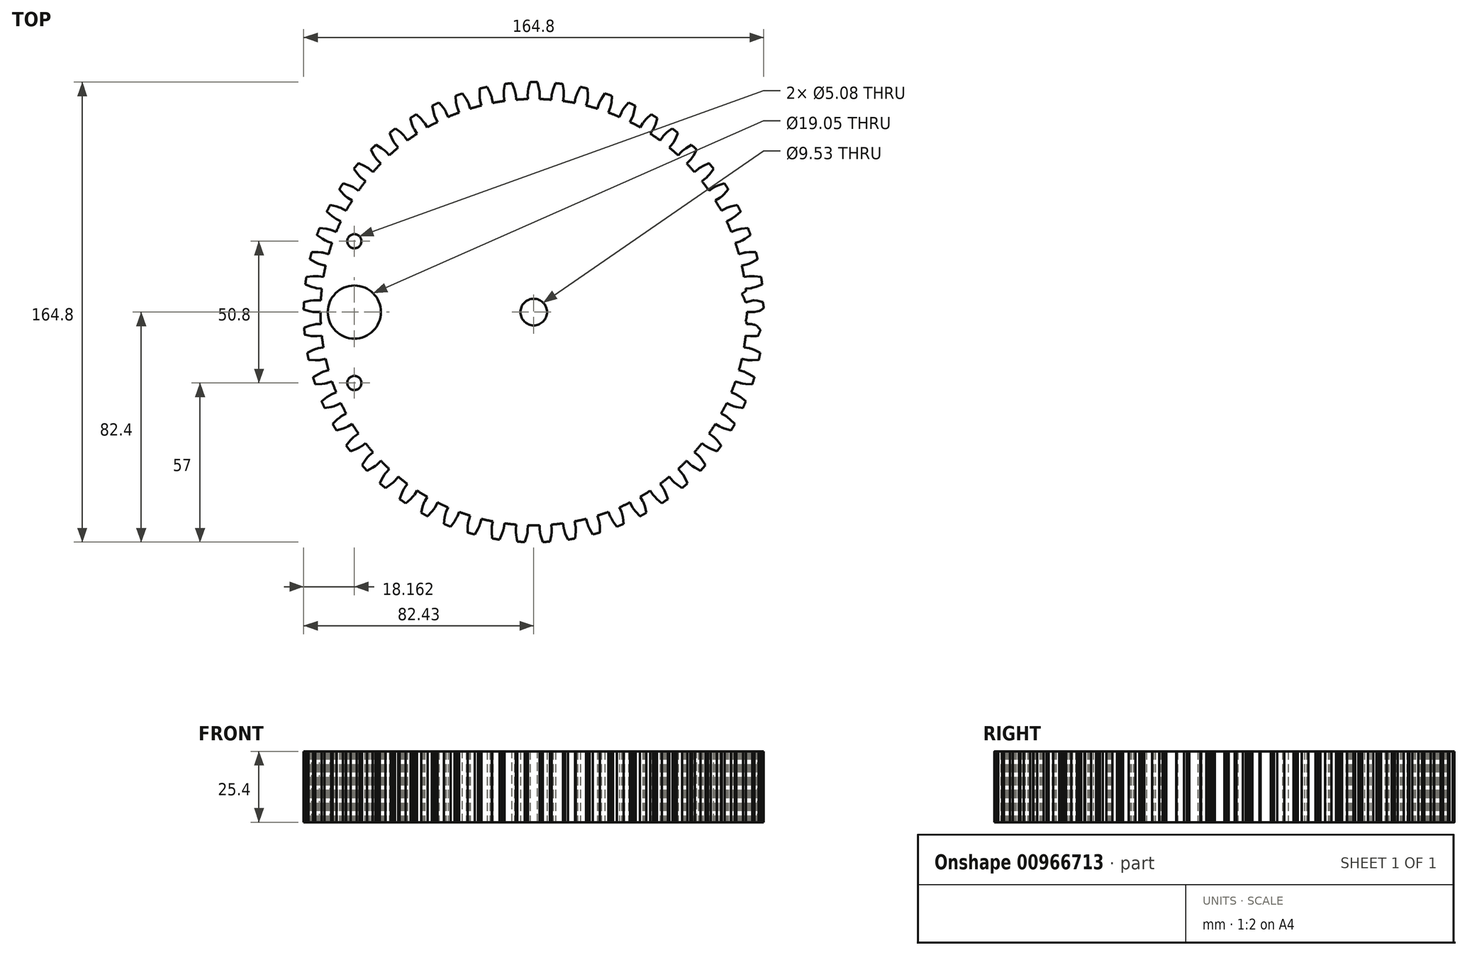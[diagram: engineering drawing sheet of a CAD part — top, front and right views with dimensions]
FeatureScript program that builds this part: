
annotation { "Feature Type Name" : "Feature", "Feature Type Description" : "" }
export const myFeature = defineFeature(function(context is Context, id is Id, definition is map)
    precondition{}
    {
        {
            var Q0;
            Q0=qCreatedBy(makeId("Top.planeOp"),FACE);
            var sketch = newSketch(context, id + "F0", { "sketchPlane" : qUnion([Q0])});
            skCircle(sketch, "E0", {"center": v(0, 0) * mm, "radius": 4.76 * mm});
            skArc(sketch, "E1", {"start": v(76.29, -4.24) * mm, "mid": v(76.37, -2.14) * mm, "end": v(76.4, -0.03) * mm});
            skLineSegment(sketch, "E2", {"start": v(76.4, -0.03) * mm, "end": v(78.17, -0.03) * mm});
            skLineSegment(sketch, "E3", {"start": v(78.17, -0.03) * mm, "end": v(78.19, -0.03) * mm});
            skLineSegment(sketch, "E4", {"start": v(78.19, -0.03) * mm, "end": v(78.2, -0.03) * mm});
            skLineSegment(sketch, "E5", {"start": v(78.2, -0.03) * mm, "end": v(78.26, -0.03) * mm});
            skLineSegment(sketch, "E6", {"start": v(78.26, -0.03) * mm, "end": v(78.37, -0.02) * mm});
            skLineSegment(sketch, "E7", {"start": v(78.37, -0.02) * mm, "end": v(78.6, 0) * mm});
            skLineSegment(sketch, "E8", {"start": v(78.6, 0) * mm, "end": v(79.09, 0.06) * mm});
            skLineSegment(sketch, "E9", {"start": v(79.09, 0.06) * mm, "end": v(80.16, 0.27) * mm});
            skLineSegment(sketch, "E10", {"start": v(80.16, 0.27) * mm, "end": v(82.43, 0.93) * mm});
            skArc(sketch, "E11", {"start": v(82.43, 0.93) * mm, "mid": v(82.4, 2.24) * mm, "end": v(82.35, 3.55) * mm});
            skLineSegment(sketch, "E12", {"start": v(78.06, 4.27) * mm, "end": v(78.07, 4.28) * mm});
            skLineSegment(sketch, "E13", {"start": v(78.07, 4.28) * mm, "end": v(78.09, 4.28) * mm});
            skLineSegment(sketch, "E14", {"start": v(78.09, 4.28) * mm, "end": v(78.14, 4.28) * mm});
            skLineSegment(sketch, "E15", {"start": v(78.14, 4.28) * mm, "end": v(78.25, 4.28) * mm});
            skLineSegment(sketch, "E16", {"start": v(78.25, 4.28) * mm, "end": v(78.47, 4.27) * mm});
            skLineSegment(sketch, "E17", {"start": v(78.47, 4.27) * mm, "end": v(78.97, 4.23) * mm});
            skLineSegment(sketch, "E18", {"start": v(78.97, 4.23) * mm, "end": v(80.05, 4.08) * mm});
            skLineSegment(sketch, "E19", {"start": v(80.05, 4.08) * mm, "end": v(82.35, 3.55) * mm});
            skLineSegment(sketch, "E20", {"start": v(76.29, 4.18) * mm, "end": v(78.06, 4.27) * mm});
            skArc(sketch, "E21", {"start": v(76.29, 4.18) * mm, "mid": v(76.14, 6.28) * mm, "end": v(75.94, 8.37) * mm});
            skLineSegment(sketch, "E22", {"start": v(75.94, 8.37) * mm, "end": v(77.7, 8.57) * mm});
            skLineSegment(sketch, "E23", {"start": v(77.7, 8.57) * mm, "end": v(77.71, 8.57) * mm});
            skLineSegment(sketch, "E24", {"start": v(77.71, 8.57) * mm, "end": v(77.73, 8.57) * mm});
            skLineSegment(sketch, "E25", {"start": v(77.73, 8.57) * mm, "end": v(77.78, 8.58) * mm});
            skLineSegment(sketch, "E26", {"start": v(77.78, 8.58) * mm, "end": v(77.89, 8.6) * mm});
            skLineSegment(sketch, "E27", {"start": v(77.89, 8.6) * mm, "end": v(78.11, 8.64) * mm});
            skLineSegment(sketch, "E28", {"start": v(78.11, 8.64) * mm, "end": v(78.6, 8.76) * mm});
            skLineSegment(sketch, "E29", {"start": v(78.6, 8.76) * mm, "end": v(79.64, 9.09) * mm});
            skLineSegment(sketch, "E30", {"start": v(79.64, 9.09) * mm, "end": v(81.82, 10) * mm});
            skArc(sketch, "E31", {"start": v(81.82, 10) * mm, "mid": v(81.65, 11.3) * mm, "end": v(81.46, 12.58) * mm});
            skLineSegment(sketch, "E32", {"start": v(77.1, 12.84) * mm, "end": v(77.12, 12.84) * mm});
            skLineSegment(sketch, "E33", {"start": v(77.12, 12.84) * mm, "end": v(77.14, 12.84) * mm});
            skLineSegment(sketch, "E34", {"start": v(77.14, 12.84) * mm, "end": v(77.2, 12.85) * mm});
            skLineSegment(sketch, "E35", {"start": v(77.2, 12.85) * mm, "end": v(77.3, 12.86) * mm});
            skLineSegment(sketch, "E36", {"start": v(77.3, 12.86) * mm, "end": v(77.52, 12.88) * mm});
            skLineSegment(sketch, "E37", {"start": v(77.52, 12.88) * mm, "end": v(78.03, 12.9) * mm});
            skLineSegment(sketch, "E38", {"start": v(78.03, 12.9) * mm, "end": v(79.11, 12.86) * mm});
            skLineSegment(sketch, "E39", {"start": v(79.11, 12.86) * mm, "end": v(81.46, 12.58) * mm});
            skLineSegment(sketch, "E40", {"start": v(75.36, 12.54) * mm, "end": v(77.1, 12.84) * mm});
            skArc(sketch, "E41", {"start": v(75.36, 12.54) * mm, "mid": v(74.99, 14.62) * mm, "end": v(74.55, 16.68) * mm});
            skLineSegment(sketch, "E42", {"start": v(74.55, 16.68) * mm, "end": v(76.28, 17.06) * mm});
            skLineSegment(sketch, "E43", {"start": v(76.28, 17.06) * mm, "end": v(76.3, 17.07) * mm});
            skLineSegment(sketch, "E44", {"start": v(76.3, 17.07) * mm, "end": v(76.31, 17.07) * mm});
            skLineSegment(sketch, "E45", {"start": v(76.31, 17.07) * mm, "end": v(76.36, 17.08) * mm});
            skLineSegment(sketch, "E46", {"start": v(76.36, 17.08) * mm, "end": v(76.47, 17.11) * mm});
            skLineSegment(sketch, "E47", {"start": v(76.47, 17.11) * mm, "end": v(76.68, 17.18) * mm});
            skLineSegment(sketch, "E48", {"start": v(76.68, 17.18) * mm, "end": v(77.15, 17.36) * mm});
            skLineSegment(sketch, "E49", {"start": v(77.15, 17.36) * mm, "end": v(78.15, 17.8) * mm});
            skLineSegment(sketch, "E50", {"start": v(78.15, 17.8) * mm, "end": v(80.22, 18.93) * mm});
            skArc(sketch, "E51", {"start": v(80.22, 18.93) * mm, "mid": v(79.9, 20.2) * mm, "end": v(79.58, 21.47) * mm});
            skLineSegment(sketch, "E52", {"start": v(75.22, 21.24) * mm, "end": v(75.24, 21.24) * mm});
            skLineSegment(sketch, "E53", {"start": v(75.24, 21.24) * mm, "end": v(75.26, 21.25) * mm});
            skLineSegment(sketch, "E54", {"start": v(75.26, 21.25) * mm, "end": v(75.3, 21.26) * mm});
            skLineSegment(sketch, "E55", {"start": v(75.3, 21.26) * mm, "end": v(75.41, 21.28) * mm});
            skLineSegment(sketch, "E56", {"start": v(75.41, 21.28) * mm, "end": v(75.63, 21.33) * mm});
            skLineSegment(sketch, "E57", {"start": v(75.63, 21.33) * mm, "end": v(76.13, 21.4) * mm});
            skLineSegment(sketch, "E58", {"start": v(76.13, 21.4) * mm, "end": v(77.22, 21.49) * mm});
            skLineSegment(sketch, "E59", {"start": v(77.22, 21.49) * mm, "end": v(79.58, 21.47) * mm});
            skLineSegment(sketch, "E60", {"start": v(73.52, 20.76) * mm, "end": v(75.22, 21.24) * mm});
            skArc(sketch, "E61", {"start": v(73.52, 20.76) * mm, "mid": v(72.92, 22.78) * mm, "end": v(72.26, 24.78) * mm});
            skLineSegment(sketch, "E62", {"start": v(72.26, 24.78) * mm, "end": v(73.94, 25.35) * mm});
            skLineSegment(sketch, "E63", {"start": v(73.94, 25.35) * mm, "end": v(73.95, 25.36) * mm});
            skLineSegment(sketch, "E64", {"start": v(73.95, 25.36) * mm, "end": v(73.97, 25.36) * mm});
            skLineSegment(sketch, "E65", {"start": v(73.97, 25.36) * mm, "end": v(74.02, 25.38) * mm});
            skLineSegment(sketch, "E66", {"start": v(74.02, 25.38) * mm, "end": v(74.12, 25.42) * mm});
            skLineSegment(sketch, "E67", {"start": v(74.12, 25.42) * mm, "end": v(74.32, 25.51) * mm});
            skLineSegment(sketch, "E68", {"start": v(74.32, 25.51) * mm, "end": v(74.77, 25.74) * mm});
            skLineSegment(sketch, "E69", {"start": v(74.77, 25.74) * mm, "end": v(75.72, 26.28) * mm});
            skLineSegment(sketch, "E70", {"start": v(75.72, 26.28) * mm, "end": v(77.65, 27.64) * mm});
            skArc(sketch, "E71", {"start": v(77.65, 27.64) * mm, "mid": v(77.2, 28.87) * mm, "end": v(76.73, 30.1) * mm});
            skLineSegment(sketch, "E72", {"start": v(72.43, 29.39) * mm, "end": v(72.44, 29.39) * mm});
            skLineSegment(sketch, "E73", {"start": v(72.44, 29.39) * mm, "end": v(72.46, 29.4) * mm});
            skLineSegment(sketch, "E74", {"start": v(72.46, 29.4) * mm, "end": v(72.5, 29.41) * mm});
            skLineSegment(sketch, "E75", {"start": v(72.5, 29.41) * mm, "end": v(72.6, 29.45) * mm});
            skLineSegment(sketch, "E76", {"start": v(72.6, 29.45) * mm, "end": v(72.83, 29.52) * mm});
            skLineSegment(sketch, "E77", {"start": v(72.83, 29.52) * mm, "end": v(73.31, 29.64) * mm});
            skLineSegment(sketch, "E78", {"start": v(73.31, 29.64) * mm, "end": v(74.38, 29.85) * mm});
            skLineSegment(sketch, "E79", {"start": v(74.38, 29.85) * mm, "end": v(76.73, 30.1) * mm});
            skLineSegment(sketch, "E80", {"start": v(70.79, 28.72) * mm, "end": v(72.43, 29.39) * mm});
            skArc(sketch, "E81", {"start": v(70.79, 28.72) * mm, "mid": v(69.97, 30.66) * mm, "end": v(69.1, 32.58) * mm});
            skLineSegment(sketch, "E82", {"start": v(69.1, 32.58) * mm, "end": v(70.7, 33.33) * mm});
            skLineSegment(sketch, "E83", {"start": v(70.7, 33.33) * mm, "end": v(70.7, 33.34) * mm});
            skLineSegment(sketch, "E84", {"start": v(70.7, 33.34) * mm, "end": v(70.73, 33.35) * mm});
            skLineSegment(sketch, "E85", {"start": v(70.73, 33.35) * mm, "end": v(70.77, 33.37) * mm});
            skLineSegment(sketch, "E86", {"start": v(70.77, 33.37) * mm, "end": v(70.87, 33.42) * mm});
            skLineSegment(sketch, "E87", {"start": v(70.87, 33.42) * mm, "end": v(71.06, 33.54) * mm});
            skLineSegment(sketch, "E88", {"start": v(71.06, 33.54) * mm, "end": v(71.48, 33.8) * mm});
            skLineSegment(sketch, "E89", {"start": v(71.48, 33.8) * mm, "end": v(72.36, 34.45) * mm});
            skLineSegment(sketch, "E90", {"start": v(72.36, 34.45) * mm, "end": v(74.13, 36.02) * mm});
            skArc(sketch, "E91", {"start": v(74.13, 36.02) * mm, "mid": v(73.55, 37.19) * mm, "end": v(72.95, 38.35) * mm});
            skLineSegment(sketch, "E92", {"start": v(68.75, 37.17) * mm, "end": v(68.76, 37.18) * mm});
            skLineSegment(sketch, "E93", {"start": v(68.76, 37.18) * mm, "end": v(68.78, 37.19) * mm});
            skLineSegment(sketch, "E94", {"start": v(68.78, 37.19) * mm, "end": v(68.83, 37.21) * mm});
            skLineSegment(sketch, "E95", {"start": v(68.83, 37.21) * mm, "end": v(68.93, 37.26) * mm});
            skLineSegment(sketch, "E96", {"start": v(68.93, 37.26) * mm, "end": v(69.13, 37.35) * mm});
            skLineSegment(sketch, "E97", {"start": v(69.13, 37.35) * mm, "end": v(69.6, 37.53) * mm});
            skLineSegment(sketch, "E98", {"start": v(69.6, 37.53) * mm, "end": v(70.64, 37.85) * mm});
            skLineSegment(sketch, "E99", {"start": v(70.64, 37.85) * mm, "end": v(72.95, 38.35) * mm});
            skLineSegment(sketch, "E100", {"start": v(67.2, 36.33) * mm, "end": v(68.75, 37.17) * mm});
            skArc(sketch, "E101", {"start": v(67.2, 36.33) * mm, "mid": v(66.17, 38.17) * mm, "end": v(65.1, 39.98) * mm});
            skLineSegment(sketch, "E102", {"start": v(65.1, 39.98) * mm, "end": v(66.6, 40.9) * mm});
            skLineSegment(sketch, "E103", {"start": v(66.6, 40.9) * mm, "end": v(66.6, 40.91) * mm});
            skLineSegment(sketch, "E104", {"start": v(66.6, 40.91) * mm, "end": v(66.62, 40.92) * mm});
            skLineSegment(sketch, "E105", {"start": v(66.62, 40.92) * mm, "end": v(66.67, 40.95) * mm});
            skLineSegment(sketch, "E106", {"start": v(66.67, 40.95) * mm, "end": v(66.76, 41.01) * mm});
            skLineSegment(sketch, "E107", {"start": v(66.76, 41.01) * mm, "end": v(66.94, 41.15) * mm});
            skLineSegment(sketch, "E108", {"start": v(66.94, 41.15) * mm, "end": v(67.33, 41.47) * mm});
            skLineSegment(sketch, "E109", {"start": v(67.33, 41.47) * mm, "end": v(68.13, 42.2) * mm});
            skLineSegment(sketch, "E110", {"start": v(68.13, 42.2) * mm, "end": v(69.71, 43.95) * mm});
            skArc(sketch, "E111", {"start": v(69.71, 43.95) * mm, "mid": v(69, 45.05) * mm, "end": v(68.29, 46.14) * mm});
            skLineSegment(sketch, "E112", {"start": v(64.24, 44.51) * mm, "end": v(64.25, 44.52) * mm});
            skLineSegment(sketch, "E113", {"start": v(64.25, 44.52) * mm, "end": v(64.27, 44.53) * mm});
            skLineSegment(sketch, "E114", {"start": v(64.27, 44.53) * mm, "end": v(64.31, 44.56) * mm});
            skLineSegment(sketch, "E115", {"start": v(64.31, 44.56) * mm, "end": v(64.4, 44.61) * mm});
            skLineSegment(sketch, "E116", {"start": v(64.4, 44.61) * mm, "end": v(64.6, 44.73) * mm});
            skLineSegment(sketch, "E117", {"start": v(64.6, 44.73) * mm, "end": v(65.05, 44.96) * mm});
            skLineSegment(sketch, "E118", {"start": v(65.05, 44.96) * mm, "end": v(66.04, 45.4) * mm});
            skLineSegment(sketch, "E119", {"start": v(66.04, 45.4) * mm, "end": v(68.29, 46.14) * mm});
            skLineSegment(sketch, "E120", {"start": v(62.79, 43.5) * mm, "end": v(64.24, 44.51) * mm});
            skArc(sketch, "E121", {"start": v(62.79, 43.5) * mm, "mid": v(61.56, 45.22) * mm, "end": v(60.3, 46.9) * mm});
            skLineSegment(sketch, "E122", {"start": v(60.3, 46.9) * mm, "end": v(61.7, 47.98) * mm});
            skLineSegment(sketch, "E123", {"start": v(61.7, 47.98) * mm, "end": v(61.7, 48) * mm});
            skLineSegment(sketch, "E124", {"start": v(61.7, 48) * mm, "end": v(61.71, 48) * mm});
            skLineSegment(sketch, "E125", {"start": v(61.71, 48) * mm, "end": v(61.75, 48.04) * mm});
            skLineSegment(sketch, "E126", {"start": v(61.75, 48.04) * mm, "end": v(61.84, 48.1) * mm});
            skLineSegment(sketch, "E127", {"start": v(61.84, 48.1) * mm, "end": v(62, 48.26) * mm});
            skLineSegment(sketch, "E128", {"start": v(62, 48.26) * mm, "end": v(62.35, 48.62) * mm});
            skLineSegment(sketch, "E129", {"start": v(62.35, 48.62) * mm, "end": v(63.07, 49.44) * mm});
            skLineSegment(sketch, "E130", {"start": v(63.07, 49.44) * mm, "end": v(64.45, 51.36) * mm});
            skArc(sketch, "E131", {"start": v(64.45, 51.36) * mm, "mid": v(63.63, 52.37) * mm, "end": v(62.8, 53.37) * mm});
            skLineSegment(sketch, "E132", {"start": v(58.95, 51.3) * mm, "end": v(58.96, 51.32) * mm});
            skLineSegment(sketch, "E133", {"start": v(58.96, 51.32) * mm, "end": v(58.98, 51.33) * mm});
            skLineSegment(sketch, "E134", {"start": v(58.98, 51.33) * mm, "end": v(59.02, 51.36) * mm});
            skLineSegment(sketch, "E135", {"start": v(59.02, 51.36) * mm, "end": v(59.1, 51.43) * mm});
            skLineSegment(sketch, "E136", {"start": v(59.1, 51.43) * mm, "end": v(59.29, 51.56) * mm});
            skLineSegment(sketch, "E137", {"start": v(59.29, 51.56) * mm, "end": v(59.7, 51.84) * mm});
            skLineSegment(sketch, "E138", {"start": v(59.7, 51.84) * mm, "end": v(60.65, 52.38) * mm});
            skLineSegment(sketch, "E139", {"start": v(60.65, 52.38) * mm, "end": v(62.8, 53.37) * mm});
            skLineSegment(sketch, "E140", {"start": v(57.62, 50.15) * mm, "end": v(58.95, 51.3) * mm});
            skArc(sketch, "E141", {"start": v(57.62, 50.15) * mm, "mid": v(56.21, 51.72) * mm, "end": v(54.77, 53.24) * mm});
            skLineSegment(sketch, "E142", {"start": v(54.77, 53.24) * mm, "end": v(56.03, 54.48) * mm});
            skLineSegment(sketch, "E143", {"start": v(56.03, 54.48) * mm, "end": v(56.04, 54.49) * mm});
            skLineSegment(sketch, "E144", {"start": v(56.04, 54.49) * mm, "end": v(56.06, 54.5) * mm});
            skLineSegment(sketch, "E145", {"start": v(56.06, 54.5) * mm, "end": v(56.1, 54.54) * mm});
            skLineSegment(sketch, "E146", {"start": v(56.1, 54.54) * mm, "end": v(56.17, 54.62) * mm});
            skLineSegment(sketch, "E147", {"start": v(56.17, 54.62) * mm, "end": v(56.31, 54.8) * mm});
            skLineSegment(sketch, "E148", {"start": v(56.31, 54.8) * mm, "end": v(56.62, 55.18) * mm});
            skLineSegment(sketch, "E149", {"start": v(56.62, 55.18) * mm, "end": v(57.24, 56.08) * mm});
            skLineSegment(sketch, "E150", {"start": v(57.24, 56.08) * mm, "end": v(58.4, 58.13) * mm});
            skArc(sketch, "E151", {"start": v(58.4, 58.13) * mm, "mid": v(57.48, 59.05) * mm, "end": v(56.53, 59.96) * mm});
            skLineSegment(sketch, "E152", {"start": v(52.95, 57.48) * mm, "end": v(52.95, 57.5) * mm});
            skLineSegment(sketch, "E153", {"start": v(52.95, 57.5) * mm, "end": v(52.97, 57.5) * mm});
            skLineSegment(sketch, "E154", {"start": v(52.97, 57.5) * mm, "end": v(53, 57.54) * mm});
            skLineSegment(sketch, "E155", {"start": v(53, 57.54) * mm, "end": v(53.08, 57.62) * mm});
            skLineSegment(sketch, "E156", {"start": v(53.08, 57.62) * mm, "end": v(53.25, 57.77) * mm});
            skLineSegment(sketch, "E157", {"start": v(53.25, 57.77) * mm, "end": v(53.63, 58.1) * mm});
            skLineSegment(sketch, "E158", {"start": v(53.63, 58.1) * mm, "end": v(54.51, 58.74) * mm});
            skLineSegment(sketch, "E159", {"start": v(54.51, 58.74) * mm, "end": v(56.53, 59.96) * mm});
            skLineSegment(sketch, "E160", {"start": v(51.75, 56.18) * mm, "end": v(52.95, 57.48) * mm});
            skArc(sketch, "E161", {"start": v(51.75, 56.18) * mm, "mid": v(50.18, 57.58) * mm, "end": v(48.57, 58.95) * mm});
            skLineSegment(sketch, "E162", {"start": v(48.57, 58.95) * mm, "end": v(49.7, 60.31) * mm});
            skLineSegment(sketch, "E163", {"start": v(49.7, 60.31) * mm, "end": v(49.7, 60.32) * mm});
            skLineSegment(sketch, "E164", {"start": v(49.7, 60.32) * mm, "end": v(49.72, 60.34) * mm});
            skLineSegment(sketch, "E165", {"start": v(49.72, 60.34) * mm, "end": v(49.75, 60.38) * mm});
            skLineSegment(sketch, "E166", {"start": v(49.75, 60.38) * mm, "end": v(49.81, 60.47) * mm});
            skLineSegment(sketch, "E167", {"start": v(49.81, 60.47) * mm, "end": v(49.94, 60.65) * mm});
            skLineSegment(sketch, "E168", {"start": v(49.94, 60.65) * mm, "end": v(50.2, 61.08) * mm});
            skLineSegment(sketch, "E169", {"start": v(50.2, 61.08) * mm, "end": v(50.72, 62.04) * mm});
            skLineSegment(sketch, "E170", {"start": v(50.72, 62.04) * mm, "end": v(51.66, 64.2) * mm});
            skArc(sketch, "E171", {"start": v(51.66, 64.2) * mm, "mid": v(50.63, 65.02) * mm, "end": v(49.6, 65.81) * mm});
            skLineSegment(sketch, "E172", {"start": v(46.3, 62.96) * mm, "end": v(46.3, 62.97) * mm});
            skLineSegment(sketch, "E173", {"start": v(46.3, 62.97) * mm, "end": v(46.32, 62.98) * mm});
            skLineSegment(sketch, "E174", {"start": v(46.32, 62.98) * mm, "end": v(46.35, 63.02) * mm});
            skLineSegment(sketch, "E175", {"start": v(46.35, 63.02) * mm, "end": v(46.42, 63.1) * mm});
            skLineSegment(sketch, "E176", {"start": v(46.42, 63.1) * mm, "end": v(46.57, 63.28) * mm});
            skLineSegment(sketch, "E177", {"start": v(46.57, 63.28) * mm, "end": v(46.92, 63.64) * mm});
            skLineSegment(sketch, "E178", {"start": v(46.92, 63.64) * mm, "end": v(47.72, 64.38) * mm});
            skLineSegment(sketch, "E179", {"start": v(47.72, 64.38) * mm, "end": v(49.6, 65.81) * mm});
            skLineSegment(sketch, "E180", {"start": v(45.25, 61.53) * mm, "end": v(46.3, 62.96) * mm});
            skArc(sketch, "E181", {"start": v(45.25, 61.53) * mm, "mid": v(43.54, 62.76) * mm, "end": v(41.79, 63.93) * mm});
            skLineSegment(sketch, "E182", {"start": v(41.79, 63.93) * mm, "end": v(42.76, 65.41) * mm});
            skLineSegment(sketch, "E183", {"start": v(42.76, 65.41) * mm, "end": v(42.76, 65.42) * mm});
            skLineSegment(sketch, "E184", {"start": v(42.76, 65.42) * mm, "end": v(42.77, 65.44) * mm});
            skLineSegment(sketch, "E185", {"start": v(42.77, 65.44) * mm, "end": v(42.8, 65.48) * mm});
            skLineSegment(sketch, "E186", {"start": v(42.8, 65.48) * mm, "end": v(42.85, 65.58) * mm});
            skLineSegment(sketch, "E187", {"start": v(42.85, 65.58) * mm, "end": v(42.96, 65.78) * mm});
            skLineSegment(sketch, "E188", {"start": v(42.96, 65.78) * mm, "end": v(43.18, 66.23) * mm});
            skLineSegment(sketch, "E189", {"start": v(43.18, 66.23) * mm, "end": v(43.59, 67.24) * mm});
            skLineSegment(sketch, "E190", {"start": v(43.59, 67.24) * mm, "end": v(44.28, 69.5) * mm});
            skArc(sketch, "E191", {"start": v(44.28, 69.5) * mm, "mid": v(43.17, 70.2) * mm, "end": v(42.05, 70.87) * mm});
            skLineSegment(sketch, "E192", {"start": v(39.09, 67.67) * mm, "end": v(39.1, 67.68) * mm});
            skLineSegment(sketch, "E193", {"start": v(39.1, 67.68) * mm, "end": v(39.1, 67.7) * mm});
            skLineSegment(sketch, "E194", {"start": v(39.1, 67.7) * mm, "end": v(39.13, 67.74) * mm});
            skLineSegment(sketch, "E195", {"start": v(39.13, 67.74) * mm, "end": v(39.2, 67.83) * mm});
            skLineSegment(sketch, "E196", {"start": v(39.2, 67.83) * mm, "end": v(39.32, 68.02) * mm});
            skLineSegment(sketch, "E197", {"start": v(39.32, 68.02) * mm, "end": v(39.63, 68.41) * mm});
            skLineSegment(sketch, "E198", {"start": v(39.63, 68.41) * mm, "end": v(40.34, 69.24) * mm});
            skLineSegment(sketch, "E199", {"start": v(40.34, 69.24) * mm, "end": v(42.05, 70.87) * mm});
            skLineSegment(sketch, "E200", {"start": v(38.2, 66.14) * mm, "end": v(39.09, 67.67) * mm});
            skArc(sketch, "E201", {"start": v(38.2, 66.14) * mm, "mid": v(36.36, 67.16) * mm, "end": v(34.5, 68.14) * mm});
            skLineSegment(sketch, "E202", {"start": v(34.5, 68.14) * mm, "end": v(35.3, 69.72) * mm});
            skLineSegment(sketch, "E203", {"start": v(35.3, 69.72) * mm, "end": v(35.3, 69.73) * mm});
            skLineSegment(sketch, "E204", {"start": v(35.3, 69.73) * mm, "end": v(35.31, 69.75) * mm});
            skLineSegment(sketch, "E205", {"start": v(35.31, 69.75) * mm, "end": v(35.33, 69.8) * mm});
            skLineSegment(sketch, "E206", {"start": v(35.33, 69.8) * mm, "end": v(35.38, 69.9) * mm});
            skLineSegment(sketch, "E207", {"start": v(35.38, 69.9) * mm, "end": v(35.46, 70.1) * mm});
            skLineSegment(sketch, "E208", {"start": v(35.46, 70.1) * mm, "end": v(35.63, 70.58) * mm});
            skLineSegment(sketch, "E209", {"start": v(35.63, 70.58) * mm, "end": v(35.92, 71.63) * mm});
            skLineSegment(sketch, "E210", {"start": v(35.92, 71.63) * mm, "end": v(36.36, 73.95) * mm});
            skArc(sketch, "E211", {"start": v(36.36, 73.95) * mm, "mid": v(35.18, 74.52) * mm, "end": v(34, 75.06) * mm});
            skLineSegment(sketch, "E212", {"start": v(31.4, 71.56) * mm, "end": v(31.4, 71.57) * mm});
            skLineSegment(sketch, "E213", {"start": v(31.4, 71.57) * mm, "end": v(31.42, 71.59) * mm});
            skLineSegment(sketch, "E214", {"start": v(31.42, 71.59) * mm, "end": v(31.44, 71.63) * mm});
            skLineSegment(sketch, "E215", {"start": v(31.44, 71.63) * mm, "end": v(31.49, 71.73) * mm});
            skLineSegment(sketch, "E216", {"start": v(31.49, 71.73) * mm, "end": v(31.6, 71.93) * mm});
            skLineSegment(sketch, "E217", {"start": v(31.6, 71.93) * mm, "end": v(31.86, 72.36) * mm});
            skLineSegment(sketch, "E218", {"start": v(31.86, 72.36) * mm, "end": v(32.48, 73.25) * mm});
            skLineSegment(sketch, "E219", {"start": v(32.48, 73.25) * mm, "end": v(34, 75.06) * mm});
            skLineSegment(sketch, "E220", {"start": v(30.7, 69.94) * mm, "end": v(31.4, 71.56) * mm});
            skArc(sketch, "E221", {"start": v(30.7, 69.94) * mm, "mid": v(28.75, 70.76) * mm, "end": v(26.8, 71.52) * mm});
            skLineSegment(sketch, "E222", {"start": v(26.8, 71.52) * mm, "end": v(27.41, 73.18) * mm});
            skLineSegment(sketch, "E223", {"start": v(27.41, 73.18) * mm, "end": v(27.41, 73.19) * mm});
            skLineSegment(sketch, "E224", {"start": v(27.41, 73.19) * mm, "end": v(27.42, 73.2) * mm});
            skLineSegment(sketch, "E225", {"start": v(27.42, 73.2) * mm, "end": v(27.44, 73.26) * mm});
            skLineSegment(sketch, "E226", {"start": v(27.44, 73.26) * mm, "end": v(27.47, 73.36) * mm});
            skLineSegment(sketch, "E227", {"start": v(27.47, 73.36) * mm, "end": v(27.53, 73.58) * mm});
            skLineSegment(sketch, "E228", {"start": v(27.53, 73.58) * mm, "end": v(27.64, 74.07) * mm});
            skLineSegment(sketch, "E229", {"start": v(27.64, 74.07) * mm, "end": v(27.82, 75.14) * mm});
            skLineSegment(sketch, "E230", {"start": v(27.82, 75.14) * mm, "end": v(28, 77.5) * mm});
            skArc(sketch, "E231", {"start": v(28, 77.5) * mm, "mid": v(26.77, 77.93) * mm, "end": v(25.53, 78.35) * mm});
            skLineSegment(sketch, "E232", {"start": v(23.34, 74.58) * mm, "end": v(23.34, 74.59) * mm});
            skLineSegment(sketch, "E233", {"start": v(23.34, 74.59) * mm, "end": v(23.35, 74.6) * mm});
            skLineSegment(sketch, "E234", {"start": v(23.35, 74.6) * mm, "end": v(23.36, 74.66) * mm});
            skLineSegment(sketch, "E235", {"start": v(23.36, 74.66) * mm, "end": v(23.4, 74.76) * mm});
            skLineSegment(sketch, "E236", {"start": v(23.4, 74.76) * mm, "end": v(23.49, 74.97) * mm});
            skLineSegment(sketch, "E237", {"start": v(23.49, 74.97) * mm, "end": v(23.7, 75.42) * mm});
            skLineSegment(sketch, "E238", {"start": v(23.7, 75.42) * mm, "end": v(24.22, 76.38) * mm});
            skLineSegment(sketch, "E239", {"start": v(24.22, 76.38) * mm, "end": v(25.53, 78.35) * mm});
            skLineSegment(sketch, "E240", {"start": v(22.8, 72.89) * mm, "end": v(23.34, 74.58) * mm});
            skArc(sketch, "E241", {"start": v(22.8, 72.89) * mm, "mid": v(20.79, 73.49) * mm, "end": v(18.76, 74.03) * mm});
            skLineSegment(sketch, "E242", {"start": v(18.76, 74.03) * mm, "end": v(19.2, 75.75) * mm});
            skLineSegment(sketch, "E243", {"start": v(19.2, 75.75) * mm, "end": v(19.2, 75.76) * mm});
            skLineSegment(sketch, "E244", {"start": v(19.2, 75.76) * mm, "end": v(19.2, 75.78) * mm});
            skLineSegment(sketch, "E245", {"start": v(19.2, 75.78) * mm, "end": v(19.2, 75.83) * mm});
            skLineSegment(sketch, "E246", {"start": v(19.2, 75.83) * mm, "end": v(19.23, 75.94) * mm});
            skLineSegment(sketch, "E247", {"start": v(19.23, 75.94) * mm, "end": v(19.27, 76.16) * mm});
            skLineSegment(sketch, "E248", {"start": v(19.27, 76.16) * mm, "end": v(19.32, 76.66) * mm});
            skLineSegment(sketch, "E249", {"start": v(19.32, 76.66) * mm, "end": v(19.38, 77.75) * mm});
            skLineSegment(sketch, "E250", {"start": v(19.38, 77.75) * mm, "end": v(19.3, 80.1) * mm});
            skArc(sketch, "E251", {"start": v(19.3, 80.1) * mm, "mid": v(18.03, 80.4) * mm, "end": v(16.75, 80.68) * mm});
            skLineSegment(sketch, "E252", {"start": v(14.99, 76.7) * mm, "end": v(14.99, 76.7) * mm});
            skLineSegment(sketch, "E253", {"start": v(14.99, 76.7) * mm, "end": v(15, 76.72) * mm});
            skLineSegment(sketch, "E254", {"start": v(15, 76.72) * mm, "end": v(15, 76.77) * mm});
            skLineSegment(sketch, "E255", {"start": v(15, 76.77) * mm, "end": v(15.03, 76.88) * mm});
            skLineSegment(sketch, "E256", {"start": v(15.03, 76.88) * mm, "end": v(15.1, 77.1) * mm});
            skLineSegment(sketch, "E257", {"start": v(15.1, 77.1) * mm, "end": v(15.25, 77.57) * mm});
            skLineSegment(sketch, "E258", {"start": v(15.25, 77.57) * mm, "end": v(15.66, 78.58) * mm});
            skLineSegment(sketch, "E259", {"start": v(15.66, 78.58) * mm, "end": v(16.75, 80.68) * mm});
            skLineSegment(sketch, "E260", {"start": v(14.65, 74.96) * mm, "end": v(14.99, 76.7) * mm});
            skArc(sketch, "E261", {"start": v(14.65, 74.96) * mm, "mid": v(12.58, 75.33) * mm, "end": v(10.5, 75.65) * mm});
            skLineSegment(sketch, "E262", {"start": v(10.5, 75.65) * mm, "end": v(10.74, 77.4) * mm});
            skLineSegment(sketch, "E263", {"start": v(10.74, 77.4) * mm, "end": v(10.74, 77.41) * mm});
            skLineSegment(sketch, "E264", {"start": v(10.74, 77.41) * mm, "end": v(10.74, 77.43) * mm});
            skLineSegment(sketch, "E265", {"start": v(10.74, 77.43) * mm, "end": v(10.75, 77.48) * mm});
            skLineSegment(sketch, "E266", {"start": v(10.75, 77.48) * mm, "end": v(10.76, 77.6) * mm});
            skLineSegment(sketch, "E267", {"start": v(10.76, 77.6) * mm, "end": v(10.77, 77.82) * mm});
            skLineSegment(sketch, "E268", {"start": v(10.77, 77.82) * mm, "end": v(10.77, 78.32) * mm});
            skLineSegment(sketch, "E269", {"start": v(10.77, 78.32) * mm, "end": v(10.71, 79.4) * mm});
            skLineSegment(sketch, "E270", {"start": v(10.71, 79.4) * mm, "end": v(10.37, 81.75) * mm});
            skArc(sketch, "E271", {"start": v(10.37, 81.75) * mm, "mid": v(9.07, 81.9) * mm, "end": v(7.77, 82.03) * mm});
            skLineSegment(sketch, "E272", {"start": v(6.46, 77.88) * mm, "end": v(6.46, 77.89) * mm});
            skLineSegment(sketch, "E273", {"start": v(6.46, 77.89) * mm, "end": v(6.46, 77.9) * mm});
            skLineSegment(sketch, "E274", {"start": v(6.46, 77.9) * mm, "end": v(6.47, 77.96) * mm});
            skLineSegment(sketch, "E275", {"start": v(6.47, 77.96) * mm, "end": v(6.48, 78.07) * mm});
            skLineSegment(sketch, "E276", {"start": v(6.48, 78.07) * mm, "end": v(6.52, 78.29) * mm});
            skLineSegment(sketch, "E277", {"start": v(6.52, 78.29) * mm, "end": v(6.62, 78.78) * mm});
            skLineSegment(sketch, "E278", {"start": v(6.62, 78.78) * mm, "end": v(6.92, 79.83) * mm});
            skLineSegment(sketch, "E279", {"start": v(6.92, 79.83) * mm, "end": v(7.77, 82.03) * mm});
            skLineSegment(sketch, "E280", {"start": v(6.3, 76.11) * mm, "end": v(6.46, 77.88) * mm});
            skArc(sketch, "E281", {"start": v(6.3, 76.11) * mm, "mid": v(4.2, 76.26) * mm, "end": v(2.1, 76.34) * mm});
            skLineSegment(sketch, "E282", {"start": v(2.1, 76.34) * mm, "end": v(2.15, 78.11) * mm});
            skLineSegment(sketch, "E283", {"start": v(2.15, 78.11) * mm, "end": v(2.15, 78.12) * mm});
            skLineSegment(sketch, "E284", {"start": v(2.15, 78.12) * mm, "end": v(2.15, 78.14) * mm});
            skLineSegment(sketch, "E285", {"start": v(2.15, 78.14) * mm, "end": v(2.15, 78.2) * mm});
            skLineSegment(sketch, "E286", {"start": v(2.15, 78.2) * mm, "end": v(2.15, 78.3) * mm});
            skLineSegment(sketch, "E287", {"start": v(2.15, 78.3) * mm, "end": v(2.14, 78.53) * mm});
            skLineSegment(sketch, "E288", {"start": v(2.14, 78.53) * mm, "end": v(2.09, 79.03) * mm});
            skLineSegment(sketch, "E289", {"start": v(2.09, 79.03) * mm, "end": v(1.9, 80.1) * mm});
            skLineSegment(sketch, "E290", {"start": v(1.9, 80.1) * mm, "end": v(1.3, 82.39) * mm});
            skArc(sketch, "E291", {"start": v(1.3, 82.39) * mm, "mid": v(0, 82.4) * mm, "end": v(-1.3, 82.39) * mm});
            skLineSegment(sketch, "E292", {"start": v(-2.15, 78.11) * mm, "end": v(-2.15, 78.12) * mm});
            skLineSegment(sketch, "E293", {"start": v(-2.15, 78.12) * mm, "end": v(-2.15, 78.14) * mm});
            skLineSegment(sketch, "E294", {"start": v(-2.15, 78.14) * mm, "end": v(-2.15, 78.2) * mm});
            skLineSegment(sketch, "E295", {"start": v(-2.15, 78.2) * mm, "end": v(-2.15, 78.3) * mm});
            skLineSegment(sketch, "E296", {"start": v(-2.15, 78.3) * mm, "end": v(-2.14, 78.53) * mm});
            skLineSegment(sketch, "E297", {"start": v(-2.14, 78.53) * mm, "end": v(-2.09, 79.03) * mm});
            skLineSegment(sketch, "E298", {"start": v(-2.09, 79.03) * mm, "end": v(-1.9, 80.1) * mm});
            skLineSegment(sketch, "E299", {"start": v(-1.9, 80.1) * mm, "end": v(-1.3, 82.39) * mm});
            skLineSegment(sketch, "E300", {"start": v(-2.1, 76.34) * mm, "end": v(-2.15, 78.11) * mm});
            skArc(sketch, "E301", {"start": v(-2.1, 76.34) * mm, "mid": v(-4.2, 76.26) * mm, "end": v(-6.3, 76.11) * mm});
            skLineSegment(sketch, "E302", {"start": v(-6.3, 76.11) * mm, "end": v(-6.46, 77.88) * mm});
            skLineSegment(sketch, "E303", {"start": v(-6.46, 77.88) * mm, "end": v(-6.46, 77.89) * mm});
            skLineSegment(sketch, "E304", {"start": v(-6.46, 77.89) * mm, "end": v(-6.46, 77.9) * mm});
            skLineSegment(sketch, "E305", {"start": v(-6.46, 77.9) * mm, "end": v(-6.47, 77.96) * mm});
            skLineSegment(sketch, "E306", {"start": v(-6.47, 77.96) * mm, "end": v(-6.48, 78.07) * mm});
            skLineSegment(sketch, "E307", {"start": v(-6.48, 78.07) * mm, "end": v(-6.52, 78.29) * mm});
            skLineSegment(sketch, "E308", {"start": v(-6.52, 78.29) * mm, "end": v(-6.62, 78.78) * mm});
            skLineSegment(sketch, "E309", {"start": v(-6.62, 78.78) * mm, "end": v(-6.92, 79.83) * mm});
            skLineSegment(sketch, "E310", {"start": v(-6.92, 79.83) * mm, "end": v(-7.77, 82.03) * mm});
            skArc(sketch, "E311", {"start": v(-7.77, 82.03) * mm, "mid": v(-9.07, 81.9) * mm, "end": v(-10.37, 81.75) * mm});
            skLineSegment(sketch, "E312", {"start": v(-10.74, 77.4) * mm, "end": v(-10.74, 77.41) * mm});
            skLineSegment(sketch, "E313", {"start": v(-10.74, 77.41) * mm, "end": v(-10.74, 77.43) * mm});
            skLineSegment(sketch, "E314", {"start": v(-10.74, 77.43) * mm, "end": v(-10.75, 77.48) * mm});
            skLineSegment(sketch, "E315", {"start": v(-10.75, 77.48) * mm, "end": v(-10.76, 77.6) * mm});
            skLineSegment(sketch, "E316", {"start": v(-10.76, 77.6) * mm, "end": v(-10.77, 77.82) * mm});
            skLineSegment(sketch, "E317", {"start": v(-10.77, 77.82) * mm, "end": v(-10.77, 78.32) * mm});
            skLineSegment(sketch, "E318", {"start": v(-10.77, 78.32) * mm, "end": v(-10.71, 79.4) * mm});
            skLineSegment(sketch, "E319", {"start": v(-10.71, 79.4) * mm, "end": v(-10.37, 81.75) * mm});
            skLineSegment(sketch, "E320", {"start": v(-10.5, 75.65) * mm, "end": v(-10.74, 77.4) * mm});
            skArc(sketch, "E321", {"start": v(-10.5, 75.65) * mm, "mid": v(-12.58, 75.33) * mm, "end": v(-14.65, 74.96) * mm});
            skLineSegment(sketch, "E322", {"start": v(-14.65, 74.96) * mm, "end": v(-14.99, 76.7) * mm});
            skLineSegment(sketch, "E323", {"start": v(-14.99, 76.7) * mm, "end": v(-14.99, 76.7) * mm});
            skLineSegment(sketch, "E324", {"start": v(-14.99, 76.7) * mm, "end": v(-15, 76.72) * mm});
            skLineSegment(sketch, "E325", {"start": v(-15, 76.72) * mm, "end": v(-15, 76.77) * mm});
            skLineSegment(sketch, "E326", {"start": v(-15, 76.77) * mm, "end": v(-15.03, 76.88) * mm});
            skLineSegment(sketch, "E327", {"start": v(-15.03, 76.88) * mm, "end": v(-15.1, 77.1) * mm});
            skLineSegment(sketch, "E328", {"start": v(-15.1, 77.1) * mm, "end": v(-15.25, 77.57) * mm});
            skLineSegment(sketch, "E329", {"start": v(-15.25, 77.57) * mm, "end": v(-15.66, 78.58) * mm});
            skLineSegment(sketch, "E330", {"start": v(-15.66, 78.58) * mm, "end": v(-16.75, 80.68) * mm});
            skArc(sketch, "E331", {"start": v(-16.75, 80.68) * mm, "mid": v(-18.03, 80.4) * mm, "end": v(-19.3, 80.1) * mm});
            skLineSegment(sketch, "E332", {"start": v(-19.2, 75.75) * mm, "end": v(-19.2, 75.76) * mm});
            skLineSegment(sketch, "E333", {"start": v(-19.2, 75.76) * mm, "end": v(-19.2, 75.78) * mm});
            skLineSegment(sketch, "E334", {"start": v(-19.2, 75.78) * mm, "end": v(-19.2, 75.83) * mm});
            skLineSegment(sketch, "E335", {"start": v(-19.2, 75.83) * mm, "end": v(-19.23, 75.94) * mm});
            skLineSegment(sketch, "E336", {"start": v(-19.23, 75.94) * mm, "end": v(-19.27, 76.16) * mm});
            skLineSegment(sketch, "E337", {"start": v(-19.27, 76.16) * mm, "end": v(-19.32, 76.66) * mm});
            skLineSegment(sketch, "E338", {"start": v(-19.32, 76.66) * mm, "end": v(-19.38, 77.75) * mm});
            skLineSegment(sketch, "E339", {"start": v(-19.38, 77.75) * mm, "end": v(-19.3, 80.1) * mm});
            skLineSegment(sketch, "E340", {"start": v(-18.76, 74.03) * mm, "end": v(-19.2, 75.75) * mm});
            skArc(sketch, "E341", {"start": v(-18.76, 74.03) * mm, "mid": v(-20.79, 73.49) * mm, "end": v(-22.8, 72.89) * mm});
            skLineSegment(sketch, "E342", {"start": v(-22.8, 72.89) * mm, "end": v(-23.34, 74.58) * mm});
            skLineSegment(sketch, "E343", {"start": v(-23.34, 74.58) * mm, "end": v(-23.34, 74.59) * mm});
            skLineSegment(sketch, "E344", {"start": v(-23.34, 74.59) * mm, "end": v(-23.35, 74.6) * mm});
            skLineSegment(sketch, "E345", {"start": v(-23.35, 74.6) * mm, "end": v(-23.36, 74.66) * mm});
            skLineSegment(sketch, "E346", {"start": v(-23.36, 74.66) * mm, "end": v(-23.4, 74.76) * mm});
            skLineSegment(sketch, "E347", {"start": v(-23.4, 74.76) * mm, "end": v(-23.49, 74.97) * mm});
            skLineSegment(sketch, "E348", {"start": v(-23.49, 74.97) * mm, "end": v(-23.7, 75.42) * mm});
            skLineSegment(sketch, "E349", {"start": v(-23.7, 75.42) * mm, "end": v(-24.22, 76.38) * mm});
            skLineSegment(sketch, "E350", {"start": v(-24.22, 76.38) * mm, "end": v(-25.53, 78.35) * mm});
            skArc(sketch, "E351", {"start": v(-25.53, 78.35) * mm, "mid": v(-26.77, 77.93) * mm, "end": v(-28, 77.5) * mm});
            skLineSegment(sketch, "E352", {"start": v(-27.41, 73.18) * mm, "end": v(-27.41, 73.19) * mm});
            skLineSegment(sketch, "E353", {"start": v(-27.41, 73.19) * mm, "end": v(-27.42, 73.2) * mm});
            skLineSegment(sketch, "E354", {"start": v(-27.42, 73.2) * mm, "end": v(-27.44, 73.26) * mm});
            skLineSegment(sketch, "E355", {"start": v(-27.44, 73.26) * mm, "end": v(-27.47, 73.36) * mm});
            skLineSegment(sketch, "E356", {"start": v(-27.47, 73.36) * mm, "end": v(-27.53, 73.58) * mm});
            skLineSegment(sketch, "E357", {"start": v(-27.53, 73.58) * mm, "end": v(-27.64, 74.07) * mm});
            skLineSegment(sketch, "E358", {"start": v(-27.64, 74.07) * mm, "end": v(-27.82, 75.14) * mm});
            skLineSegment(sketch, "E359", {"start": v(-27.82, 75.14) * mm, "end": v(-28, 77.5) * mm});
            skLineSegment(sketch, "E360", {"start": v(-26.8, 71.52) * mm, "end": v(-27.41, 73.18) * mm});
            skArc(sketch, "E361", {"start": v(-26.8, 71.52) * mm, "mid": v(-28.75, 70.76) * mm, "end": v(-30.7, 69.94) * mm});
            skLineSegment(sketch, "E362", {"start": v(-30.7, 69.94) * mm, "end": v(-31.4, 71.56) * mm});
            skLineSegment(sketch, "E363", {"start": v(-31.4, 71.56) * mm, "end": v(-31.4, 71.57) * mm});
            skLineSegment(sketch, "E364", {"start": v(-31.4, 71.57) * mm, "end": v(-31.42, 71.59) * mm});
            skLineSegment(sketch, "E365", {"start": v(-31.42, 71.59) * mm, "end": v(-31.44, 71.63) * mm});
            skLineSegment(sketch, "E366", {"start": v(-31.44, 71.63) * mm, "end": v(-31.49, 71.73) * mm});
            skLineSegment(sketch, "E367", {"start": v(-31.49, 71.73) * mm, "end": v(-31.6, 71.93) * mm});
            skLineSegment(sketch, "E368", {"start": v(-31.6, 71.93) * mm, "end": v(-31.86, 72.36) * mm});
            skLineSegment(sketch, "E369", {"start": v(-31.86, 72.36) * mm, "end": v(-32.48, 73.25) * mm});
            skLineSegment(sketch, "E370", {"start": v(-32.48, 73.25) * mm, "end": v(-34, 75.06) * mm});
            skArc(sketch, "E371", {"start": v(-34, 75.06) * mm, "mid": v(-35.18, 74.52) * mm, "end": v(-36.36, 73.95) * mm});
            skLineSegment(sketch, "E372", {"start": v(-35.3, 69.72) * mm, "end": v(-35.3, 69.73) * mm});
            skLineSegment(sketch, "E373", {"start": v(-35.3, 69.73) * mm, "end": v(-35.31, 69.75) * mm});
            skLineSegment(sketch, "E374", {"start": v(-35.31, 69.75) * mm, "end": v(-35.33, 69.8) * mm});
            skLineSegment(sketch, "E375", {"start": v(-35.33, 69.8) * mm, "end": v(-35.38, 69.9) * mm});
            skLineSegment(sketch, "E376", {"start": v(-35.38, 69.9) * mm, "end": v(-35.46, 70.1) * mm});
            skLineSegment(sketch, "E377", {"start": v(-35.46, 70.1) * mm, "end": v(-35.63, 70.58) * mm});
            skLineSegment(sketch, "E378", {"start": v(-35.63, 70.58) * mm, "end": v(-35.92, 71.63) * mm});
            skLineSegment(sketch, "E379", {"start": v(-35.92, 71.63) * mm, "end": v(-36.36, 73.95) * mm});
            skLineSegment(sketch, "E380", {"start": v(-34.5, 68.14) * mm, "end": v(-35.3, 69.72) * mm});
            skArc(sketch, "E381", {"start": v(-34.5, 68.14) * mm, "mid": v(-36.36, 67.16) * mm, "end": v(-38.2, 66.14) * mm});
            skLineSegment(sketch, "E382", {"start": v(-38.2, 66.14) * mm, "end": v(-39.09, 67.67) * mm});
            skLineSegment(sketch, "E383", {"start": v(-39.09, 67.67) * mm, "end": v(-39.1, 67.68) * mm});
            skLineSegment(sketch, "E384", {"start": v(-39.1, 67.68) * mm, "end": v(-39.1, 67.7) * mm});
            skLineSegment(sketch, "E385", {"start": v(-39.1, 67.7) * mm, "end": v(-39.13, 67.74) * mm});
            skLineSegment(sketch, "E386", {"start": v(-39.13, 67.74) * mm, "end": v(-39.2, 67.83) * mm});
            skLineSegment(sketch, "E387", {"start": v(-39.2, 67.83) * mm, "end": v(-39.32, 68.02) * mm});
            skLineSegment(sketch, "E388", {"start": v(-39.32, 68.02) * mm, "end": v(-39.63, 68.41) * mm});
            skLineSegment(sketch, "E389", {"start": v(-39.63, 68.41) * mm, "end": v(-40.34, 69.24) * mm});
            skLineSegment(sketch, "E390", {"start": v(-40.34, 69.24) * mm, "end": v(-42.05, 70.87) * mm});
            skArc(sketch, "E391", {"start": v(-42.05, 70.87) * mm, "mid": v(-43.17, 70.2) * mm, "end": v(-44.28, 69.5) * mm});
            skLineSegment(sketch, "E392", {"start": v(-42.76, 65.41) * mm, "end": v(-42.76, 65.42) * mm});
            skLineSegment(sketch, "E393", {"start": v(-42.76, 65.42) * mm, "end": v(-42.77, 65.44) * mm});
            skLineSegment(sketch, "E394", {"start": v(-42.77, 65.44) * mm, "end": v(-42.8, 65.48) * mm});
            skLineSegment(sketch, "E395", {"start": v(-42.8, 65.48) * mm, "end": v(-42.85, 65.58) * mm});
            skLineSegment(sketch, "E396", {"start": v(-42.85, 65.58) * mm, "end": v(-42.96, 65.78) * mm});
            skLineSegment(sketch, "E397", {"start": v(-42.96, 65.78) * mm, "end": v(-43.18, 66.23) * mm});
            skLineSegment(sketch, "E398", {"start": v(-43.18, 66.23) * mm, "end": v(-43.59, 67.24) * mm});
            skLineSegment(sketch, "E399", {"start": v(-43.59, 67.24) * mm, "end": v(-44.28, 69.5) * mm});
            skLineSegment(sketch, "E400", {"start": v(-41.79, 63.93) * mm, "end": v(-42.76, 65.41) * mm});
            skArc(sketch, "E401", {"start": v(-41.79, 63.93) * mm, "mid": v(-43.54, 62.76) * mm, "end": v(-45.25, 61.53) * mm});
            skLineSegment(sketch, "E402", {"start": v(-45.25, 61.53) * mm, "end": v(-46.3, 62.96) * mm});
            skLineSegment(sketch, "E403", {"start": v(-46.3, 62.96) * mm, "end": v(-46.3, 62.97) * mm});
            skLineSegment(sketch, "E404", {"start": v(-46.3, 62.97) * mm, "end": v(-46.32, 62.98) * mm});
            skLineSegment(sketch, "E405", {"start": v(-46.32, 62.98) * mm, "end": v(-46.35, 63.02) * mm});
            skLineSegment(sketch, "E406", {"start": v(-46.35, 63.02) * mm, "end": v(-46.42, 63.1) * mm});
            skLineSegment(sketch, "E407", {"start": v(-46.42, 63.1) * mm, "end": v(-46.57, 63.28) * mm});
            skLineSegment(sketch, "E408", {"start": v(-46.57, 63.28) * mm, "end": v(-46.92, 63.64) * mm});
            skLineSegment(sketch, "E409", {"start": v(-46.92, 63.64) * mm, "end": v(-47.72, 64.38) * mm});
            skLineSegment(sketch, "E410", {"start": v(-47.72, 64.38) * mm, "end": v(-49.6, 65.81) * mm});
            skArc(sketch, "E411", {"start": v(-49.6, 65.81) * mm, "mid": v(-50.63, 65.02) * mm, "end": v(-51.66, 64.2) * mm});
            skLineSegment(sketch, "E412", {"start": v(-49.7, 60.31) * mm, "end": v(-49.7, 60.32) * mm});
            skLineSegment(sketch, "E413", {"start": v(-49.7, 60.32) * mm, "end": v(-49.72, 60.34) * mm});
            skLineSegment(sketch, "E414", {"start": v(-49.72, 60.34) * mm, "end": v(-49.75, 60.38) * mm});
            skLineSegment(sketch, "E415", {"start": v(-49.75, 60.38) * mm, "end": v(-49.81, 60.47) * mm});
            skLineSegment(sketch, "E416", {"start": v(-49.81, 60.47) * mm, "end": v(-49.94, 60.65) * mm});
            skLineSegment(sketch, "E417", {"start": v(-49.94, 60.65) * mm, "end": v(-50.2, 61.08) * mm});
            skLineSegment(sketch, "E418", {"start": v(-50.2, 61.08) * mm, "end": v(-50.72, 62.04) * mm});
            skLineSegment(sketch, "E419", {"start": v(-50.72, 62.04) * mm, "end": v(-51.66, 64.2) * mm});
            skLineSegment(sketch, "E420", {"start": v(-48.57, 58.95) * mm, "end": v(-49.7, 60.31) * mm});
            skArc(sketch, "E421", {"start": v(-48.57, 58.95) * mm, "mid": v(-50.18, 57.58) * mm, "end": v(-51.75, 56.18) * mm});
            skLineSegment(sketch, "E422", {"start": v(-51.75, 56.18) * mm, "end": v(-52.95, 57.48) * mm});
            skLineSegment(sketch, "E423", {"start": v(-52.95, 57.48) * mm, "end": v(-52.95, 57.5) * mm});
            skLineSegment(sketch, "E424", {"start": v(-52.95, 57.5) * mm, "end": v(-52.97, 57.5) * mm});
            skLineSegment(sketch, "E425", {"start": v(-52.97, 57.5) * mm, "end": v(-53, 57.54) * mm});
            skLineSegment(sketch, "E426", {"start": v(-53, 57.54) * mm, "end": v(-53.08, 57.62) * mm});
            skLineSegment(sketch, "E427", {"start": v(-53.08, 57.62) * mm, "end": v(-53.25, 57.77) * mm});
            skLineSegment(sketch, "E428", {"start": v(-53.25, 57.77) * mm, "end": v(-53.63, 58.1) * mm});
            skLineSegment(sketch, "E429", {"start": v(-53.63, 58.1) * mm, "end": v(-54.51, 58.74) * mm});
            skLineSegment(sketch, "E430", {"start": v(-54.51, 58.74) * mm, "end": v(-56.53, 59.96) * mm});
            skArc(sketch, "E431", {"start": v(-56.53, 59.96) * mm, "mid": v(-57.48, 59.05) * mm, "end": v(-58.4, 58.13) * mm});
            skLineSegment(sketch, "E432", {"start": v(-56.03, 54.48) * mm, "end": v(-56.04, 54.49) * mm});
            skLineSegment(sketch, "E433", {"start": v(-56.04, 54.49) * mm, "end": v(-56.06, 54.5) * mm});
            skLineSegment(sketch, "E434", {"start": v(-56.06, 54.5) * mm, "end": v(-56.1, 54.54) * mm});
            skLineSegment(sketch, "E435", {"start": v(-56.1, 54.54) * mm, "end": v(-56.17, 54.62) * mm});
            skLineSegment(sketch, "E436", {"start": v(-56.17, 54.62) * mm, "end": v(-56.31, 54.8) * mm});
            skLineSegment(sketch, "E437", {"start": v(-56.31, 54.8) * mm, "end": v(-56.62, 55.18) * mm});
            skLineSegment(sketch, "E438", {"start": v(-56.62, 55.18) * mm, "end": v(-57.24, 56.08) * mm});
            skLineSegment(sketch, "E439", {"start": v(-57.24, 56.08) * mm, "end": v(-58.4, 58.13) * mm});
            skLineSegment(sketch, "E440", {"start": v(-54.77, 53.24) * mm, "end": v(-56.03, 54.48) * mm});
            skArc(sketch, "E441", {"start": v(-54.77, 53.24) * mm, "mid": v(-56.21, 51.72) * mm, "end": v(-57.62, 50.15) * mm});
            skLineSegment(sketch, "E442", {"start": v(-57.62, 50.15) * mm, "end": v(-58.95, 51.3) * mm});
            skLineSegment(sketch, "E443", {"start": v(-58.95, 51.3) * mm, "end": v(-58.96, 51.32) * mm});
            skLineSegment(sketch, "E444", {"start": v(-58.96, 51.32) * mm, "end": v(-58.98, 51.33) * mm});
            skLineSegment(sketch, "E445", {"start": v(-58.98, 51.33) * mm, "end": v(-59.02, 51.36) * mm});
            skLineSegment(sketch, "E446", {"start": v(-59.02, 51.36) * mm, "end": v(-59.1, 51.43) * mm});
            skLineSegment(sketch, "E447", {"start": v(-59.1, 51.43) * mm, "end": v(-59.29, 51.56) * mm});
            skLineSegment(sketch, "E448", {"start": v(-59.29, 51.56) * mm, "end": v(-59.7, 51.84) * mm});
            skLineSegment(sketch, "E449", {"start": v(-59.7, 51.84) * mm, "end": v(-60.65, 52.38) * mm});
            skLineSegment(sketch, "E450", {"start": v(-60.65, 52.38) * mm, "end": v(-62.8, 53.37) * mm});
            skArc(sketch, "E451", {"start": v(-62.8, 53.37) * mm, "mid": v(-63.63, 52.37) * mm, "end": v(-64.45, 51.36) * mm});
            skLineSegment(sketch, "E452", {"start": v(-61.7, 47.98) * mm, "end": v(-61.7, 48) * mm});
            skLineSegment(sketch, "E453", {"start": v(-61.7, 48) * mm, "end": v(-61.71, 48) * mm});
            skLineSegment(sketch, "E454", {"start": v(-61.71, 48) * mm, "end": v(-61.75, 48.04) * mm});
            skLineSegment(sketch, "E455", {"start": v(-61.75, 48.04) * mm, "end": v(-61.84, 48.1) * mm});
            skLineSegment(sketch, "E456", {"start": v(-61.84, 48.1) * mm, "end": v(-62, 48.26) * mm});
            skLineSegment(sketch, "E457", {"start": v(-62, 48.26) * mm, "end": v(-62.35, 48.62) * mm});
            skLineSegment(sketch, "E458", {"start": v(-62.35, 48.62) * mm, "end": v(-63.07, 49.44) * mm});
            skLineSegment(sketch, "E459", {"start": v(-63.07, 49.44) * mm, "end": v(-64.45, 51.36) * mm});
            skLineSegment(sketch, "E460", {"start": v(-60.3, 46.9) * mm, "end": v(-61.7, 47.98) * mm});
            skArc(sketch, "E461", {"start": v(-60.3, 46.9) * mm, "mid": v(-61.56, 45.22) * mm, "end": v(-62.79, 43.5) * mm});
            skLineSegment(sketch, "E462", {"start": v(-62.79, 43.5) * mm, "end": v(-64.24, 44.51) * mm});
            skLineSegment(sketch, "E463", {"start": v(-64.24, 44.51) * mm, "end": v(-64.25, 44.52) * mm});
            skLineSegment(sketch, "E464", {"start": v(-64.25, 44.52) * mm, "end": v(-64.27, 44.53) * mm});
            skLineSegment(sketch, "E465", {"start": v(-64.27, 44.53) * mm, "end": v(-64.31, 44.56) * mm});
            skLineSegment(sketch, "E466", {"start": v(-64.31, 44.56) * mm, "end": v(-64.4, 44.61) * mm});
            skLineSegment(sketch, "E467", {"start": v(-64.4, 44.61) * mm, "end": v(-64.6, 44.73) * mm});
            skLineSegment(sketch, "E468", {"start": v(-64.6, 44.73) * mm, "end": v(-65.05, 44.96) * mm});
            skLineSegment(sketch, "E469", {"start": v(-65.05, 44.96) * mm, "end": v(-66.04, 45.4) * mm});
            skLineSegment(sketch, "E470", {"start": v(-66.04, 45.4) * mm, "end": v(-68.29, 46.14) * mm});
            skArc(sketch, "E471", {"start": v(-68.29, 46.14) * mm, "mid": v(-69, 45.05) * mm, "end": v(-69.71, 43.95) * mm});
            skLineSegment(sketch, "E472", {"start": v(-66.6, 40.9) * mm, "end": v(-66.6, 40.91) * mm});
            skLineSegment(sketch, "E473", {"start": v(-66.6, 40.91) * mm, "end": v(-66.62, 40.92) * mm});
            skLineSegment(sketch, "E474", {"start": v(-66.62, 40.92) * mm, "end": v(-66.67, 40.95) * mm});
            skLineSegment(sketch, "E475", {"start": v(-66.67, 40.95) * mm, "end": v(-66.76, 41.01) * mm});
            skLineSegment(sketch, "E476", {"start": v(-66.76, 41.01) * mm, "end": v(-66.94, 41.15) * mm});
            skLineSegment(sketch, "E477", {"start": v(-66.94, 41.15) * mm, "end": v(-67.33, 41.47) * mm});
            skLineSegment(sketch, "E478", {"start": v(-67.33, 41.47) * mm, "end": v(-68.13, 42.2) * mm});
            skLineSegment(sketch, "E479", {"start": v(-68.13, 42.2) * mm, "end": v(-69.71, 43.95) * mm});
            skLineSegment(sketch, "E480", {"start": v(-65.1, 39.98) * mm, "end": v(-66.6, 40.9) * mm});
            skArc(sketch, "E481", {"start": v(-65.1, 39.98) * mm, "mid": v(-66.17, 38.17) * mm, "end": v(-67.2, 36.33) * mm});
            skLineSegment(sketch, "E482", {"start": v(-67.2, 36.33) * mm, "end": v(-68.75, 37.17) * mm});
            skLineSegment(sketch, "E483", {"start": v(-68.75, 37.17) * mm, "end": v(-68.76, 37.18) * mm});
            skLineSegment(sketch, "E484", {"start": v(-68.76, 37.18) * mm, "end": v(-68.78, 37.19) * mm});
            skLineSegment(sketch, "E485", {"start": v(-68.78, 37.19) * mm, "end": v(-68.83, 37.21) * mm});
            skLineSegment(sketch, "E486", {"start": v(-68.83, 37.21) * mm, "end": v(-68.93, 37.26) * mm});
            skLineSegment(sketch, "E487", {"start": v(-68.93, 37.26) * mm, "end": v(-69.13, 37.35) * mm});
            skLineSegment(sketch, "E488", {"start": v(-69.13, 37.35) * mm, "end": v(-69.6, 37.53) * mm});
            skLineSegment(sketch, "E489", {"start": v(-69.6, 37.53) * mm, "end": v(-70.64, 37.85) * mm});
            skLineSegment(sketch, "E490", {"start": v(-70.64, 37.85) * mm, "end": v(-72.95, 38.35) * mm});
            skArc(sketch, "E491", {"start": v(-72.95, 38.35) * mm, "mid": v(-73.55, 37.19) * mm, "end": v(-74.13, 36.02) * mm});
            skLineSegment(sketch, "E492", {"start": v(-70.7, 33.33) * mm, "end": v(-70.7, 33.34) * mm});
            skLineSegment(sketch, "E493", {"start": v(-70.7, 33.34) * mm, "end": v(-70.73, 33.35) * mm});
            skLineSegment(sketch, "E494", {"start": v(-70.73, 33.35) * mm, "end": v(-70.77, 33.37) * mm});
            skLineSegment(sketch, "E495", {"start": v(-70.77, 33.37) * mm, "end": v(-70.87, 33.42) * mm});
            skLineSegment(sketch, "E496", {"start": v(-70.87, 33.42) * mm, "end": v(-71.06, 33.54) * mm});
            skLineSegment(sketch, "E497", {"start": v(-71.06, 33.54) * mm, "end": v(-71.48, 33.8) * mm});
            skLineSegment(sketch, "E498", {"start": v(-71.48, 33.8) * mm, "end": v(-72.36, 34.45) * mm});
            skLineSegment(sketch, "E499", {"start": v(-72.36, 34.45) * mm, "end": v(-74.13, 36.02) * mm});
            skLineSegment(sketch, "E500", {"start": v(-69.1, 32.58) * mm, "end": v(-70.7, 33.33) * mm});
            skArc(sketch, "E501", {"start": v(-69.1, 32.58) * mm, "mid": v(-69.97, 30.66) * mm, "end": v(-70.79, 28.72) * mm});
            skLineSegment(sketch, "E502", {"start": v(-70.79, 28.72) * mm, "end": v(-72.43, 29.39) * mm});
            skLineSegment(sketch, "E503", {"start": v(-72.43, 29.39) * mm, "end": v(-72.44, 29.39) * mm});
            skLineSegment(sketch, "E504", {"start": v(-72.44, 29.39) * mm, "end": v(-72.46, 29.4) * mm});
            skLineSegment(sketch, "E505", {"start": v(-72.46, 29.4) * mm, "end": v(-72.5, 29.41) * mm});
            skLineSegment(sketch, "E506", {"start": v(-72.5, 29.41) * mm, "end": v(-72.6, 29.45) * mm});
            skLineSegment(sketch, "E507", {"start": v(-72.6, 29.45) * mm, "end": v(-72.83, 29.52) * mm});
            skLineSegment(sketch, "E508", {"start": v(-72.83, 29.52) * mm, "end": v(-73.31, 29.64) * mm});
            skLineSegment(sketch, "E509", {"start": v(-73.31, 29.64) * mm, "end": v(-74.38, 29.85) * mm});
            skLineSegment(sketch, "E510", {"start": v(-74.38, 29.85) * mm, "end": v(-76.73, 30.1) * mm});
            skArc(sketch, "E511", {"start": v(-76.73, 30.1) * mm, "mid": v(-77.2, 28.87) * mm, "end": v(-77.65, 27.64) * mm});
            skLineSegment(sketch, "E512", {"start": v(-73.94, 25.35) * mm, "end": v(-73.95, 25.36) * mm});
            skLineSegment(sketch, "E513", {"start": v(-73.95, 25.36) * mm, "end": v(-73.97, 25.36) * mm});
            skLineSegment(sketch, "E514", {"start": v(-73.97, 25.36) * mm, "end": v(-74.02, 25.38) * mm});
            skLineSegment(sketch, "E515", {"start": v(-74.02, 25.38) * mm, "end": v(-74.12, 25.42) * mm});
            skLineSegment(sketch, "E516", {"start": v(-74.12, 25.42) * mm, "end": v(-74.32, 25.51) * mm});
            skLineSegment(sketch, "E517", {"start": v(-74.32, 25.51) * mm, "end": v(-74.77, 25.74) * mm});
            skLineSegment(sketch, "E518", {"start": v(-74.77, 25.74) * mm, "end": v(-75.72, 26.28) * mm});
            skLineSegment(sketch, "E519", {"start": v(-75.72, 26.28) * mm, "end": v(-77.65, 27.64) * mm});
            skLineSegment(sketch, "E520", {"start": v(-72.26, 24.78) * mm, "end": v(-73.94, 25.35) * mm});
            skArc(sketch, "E521", {"start": v(-72.26, 24.78) * mm, "mid": v(-72.92, 22.78) * mm, "end": v(-73.52, 20.76) * mm});
            skLineSegment(sketch, "E522", {"start": v(-73.52, 20.76) * mm, "end": v(-75.22, 21.24) * mm});
            skLineSegment(sketch, "E523", {"start": v(-75.22, 21.24) * mm, "end": v(-75.24, 21.24) * mm});
            skLineSegment(sketch, "E524", {"start": v(-75.24, 21.24) * mm, "end": v(-75.26, 21.25) * mm});
            skLineSegment(sketch, "E525", {"start": v(-75.26, 21.25) * mm, "end": v(-75.3, 21.26) * mm});
            skLineSegment(sketch, "E526", {"start": v(-75.3, 21.26) * mm, "end": v(-75.41, 21.28) * mm});
            skLineSegment(sketch, "E527", {"start": v(-75.41, 21.28) * mm, "end": v(-75.63, 21.33) * mm});
            skLineSegment(sketch, "E528", {"start": v(-75.63, 21.33) * mm, "end": v(-76.13, 21.4) * mm});
            skLineSegment(sketch, "E529", {"start": v(-76.13, 21.4) * mm, "end": v(-77.22, 21.49) * mm});
            skLineSegment(sketch, "E530", {"start": v(-77.22, 21.49) * mm, "end": v(-79.58, 21.47) * mm});
            skArc(sketch, "E531", {"start": v(-79.58, 21.47) * mm, "mid": v(-79.9, 20.2) * mm, "end": v(-80.22, 18.93) * mm});
            skLineSegment(sketch, "E532", {"start": v(-76.28, 17.06) * mm, "end": v(-76.3, 17.07) * mm});
            skLineSegment(sketch, "E533", {"start": v(-76.3, 17.07) * mm, "end": v(-76.31, 17.07) * mm});
            skLineSegment(sketch, "E534", {"start": v(-76.31, 17.07) * mm, "end": v(-76.36, 17.08) * mm});
            skLineSegment(sketch, "E535", {"start": v(-76.36, 17.08) * mm, "end": v(-76.47, 17.11) * mm});
            skLineSegment(sketch, "E536", {"start": v(-76.47, 17.11) * mm, "end": v(-76.68, 17.18) * mm});
            skLineSegment(sketch, "E537", {"start": v(-76.68, 17.18) * mm, "end": v(-77.15, 17.36) * mm});
            skLineSegment(sketch, "E538", {"start": v(-77.15, 17.36) * mm, "end": v(-78.15, 17.8) * mm});
            skLineSegment(sketch, "E539", {"start": v(-78.15, 17.8) * mm, "end": v(-80.22, 18.93) * mm});
            skLineSegment(sketch, "E540", {"start": v(-74.55, 16.68) * mm, "end": v(-76.28, 17.06) * mm});
            skArc(sketch, "E541", {"start": v(-74.55, 16.68) * mm, "mid": v(-74.99, 14.62) * mm, "end": v(-75.36, 12.54) * mm});
            skLineSegment(sketch, "E542", {"start": v(-75.36, 12.54) * mm, "end": v(-77.1, 12.84) * mm});
            skLineSegment(sketch, "E543", {"start": v(-77.1, 12.84) * mm, "end": v(-77.12, 12.84) * mm});
            skLineSegment(sketch, "E544", {"start": v(-77.12, 12.84) * mm, "end": v(-77.14, 12.84) * mm});
            skLineSegment(sketch, "E545", {"start": v(-77.14, 12.84) * mm, "end": v(-77.2, 12.85) * mm});
            skLineSegment(sketch, "E546", {"start": v(-77.2, 12.85) * mm, "end": v(-77.3, 12.86) * mm});
            skLineSegment(sketch, "E547", {"start": v(-77.3, 12.86) * mm, "end": v(-77.52, 12.88) * mm});
            skLineSegment(sketch, "E548", {"start": v(-77.52, 12.88) * mm, "end": v(-78.03, 12.9) * mm});
            skLineSegment(sketch, "E549", {"start": v(-78.03, 12.9) * mm, "end": v(-79.11, 12.86) * mm});
            skLineSegment(sketch, "E550", {"start": v(-79.11, 12.86) * mm, "end": v(-81.46, 12.58) * mm});
            skArc(sketch, "E551", {"start": v(-81.46, 12.58) * mm, "mid": v(-81.65, 11.3) * mm, "end": v(-81.82, 10) * mm});
            skLineSegment(sketch, "E552", {"start": v(-77.7, 8.57) * mm, "end": v(-77.71, 8.57) * mm});
            skLineSegment(sketch, "E553", {"start": v(-77.71, 8.57) * mm, "end": v(-77.73, 8.57) * mm});
            skLineSegment(sketch, "E554", {"start": v(-77.73, 8.57) * mm, "end": v(-77.78, 8.58) * mm});
            skLineSegment(sketch, "E555", {"start": v(-77.78, 8.58) * mm, "end": v(-77.89, 8.6) * mm});
            skLineSegment(sketch, "E556", {"start": v(-77.89, 8.6) * mm, "end": v(-78.11, 8.64) * mm});
            skLineSegment(sketch, "E557", {"start": v(-78.11, 8.64) * mm, "end": v(-78.6, 8.76) * mm});
            skLineSegment(sketch, "E558", {"start": v(-78.6, 8.76) * mm, "end": v(-79.64, 9.09) * mm});
            skLineSegment(sketch, "E559", {"start": v(-79.64, 9.09) * mm, "end": v(-81.82, 10) * mm});
            skLineSegment(sketch, "E560", {"start": v(-75.94, 8.37) * mm, "end": v(-77.7, 8.57) * mm});
            skArc(sketch, "E561", {"start": v(-75.94, 8.37) * mm, "mid": v(-76.14, 6.28) * mm, "end": v(-76.29, 4.18) * mm});
            skLineSegment(sketch, "E562", {"start": v(-76.29, 4.18) * mm, "end": v(-78.06, 4.27) * mm});
            skLineSegment(sketch, "E563", {"start": v(-78.06, 4.27) * mm, "end": v(-78.07, 4.28) * mm});
            skLineSegment(sketch, "E564", {"start": v(-78.07, 4.28) * mm, "end": v(-78.09, 4.28) * mm});
            skLineSegment(sketch, "E565", {"start": v(-78.09, 4.28) * mm, "end": v(-78.14, 4.28) * mm});
            skLineSegment(sketch, "E566", {"start": v(-78.14, 4.28) * mm, "end": v(-78.25, 4.28) * mm});
            skLineSegment(sketch, "E567", {"start": v(-78.25, 4.28) * mm, "end": v(-78.47, 4.27) * mm});
            skLineSegment(sketch, "E568", {"start": v(-78.47, 4.27) * mm, "end": v(-78.97, 4.23) * mm});
            skLineSegment(sketch, "E569", {"start": v(-78.97, 4.23) * mm, "end": v(-80.05, 4.08) * mm});
            skLineSegment(sketch, "E570", {"start": v(-80.05, 4.08) * mm, "end": v(-82.35, 3.55) * mm});
            skArc(sketch, "E571", {"start": v(-82.35, 3.55) * mm, "mid": v(-82.4, 2.24) * mm, "end": v(-82.43, 0.93) * mm});
            skLineSegment(sketch, "E572", {"start": v(-78.17, -0.03) * mm, "end": v(-78.19, -0.03) * mm});
            skLineSegment(sketch, "E573", {"start": v(-78.19, -0.03) * mm, "end": v(-78.2, -0.03) * mm});
            skLineSegment(sketch, "E574", {"start": v(-78.2, -0.03) * mm, "end": v(-78.26, -0.03) * mm});
            skLineSegment(sketch, "E575", {"start": v(-78.26, -0.03) * mm, "end": v(-78.37, -0.02) * mm});
            skLineSegment(sketch, "E576", {"start": v(-78.37, -0.02) * mm, "end": v(-78.6, 0) * mm});
            skLineSegment(sketch, "E577", {"start": v(-78.6, 0) * mm, "end": v(-79.09, 0.06) * mm});
            skLineSegment(sketch, "E578", {"start": v(-79.09, 0.06) * mm, "end": v(-80.16, 0.27) * mm});
            skLineSegment(sketch, "E579", {"start": v(-80.16, 0.27) * mm, "end": v(-82.43, 0.93) * mm});
            skLineSegment(sketch, "E580", {"start": v(-76.4, -0.03) * mm, "end": v(-78.17, -0.03) * mm});
            skArc(sketch, "E581", {"start": v(-76.4, -0.03) * mm, "mid": v(-76.37, -2.14) * mm, "end": v(-76.29, -4.24) * mm});
            skLineSegment(sketch, "E582", {"start": v(-76.29, -4.24) * mm, "end": v(-78.06, -4.34) * mm});
            skLineSegment(sketch, "E583", {"start": v(-78.06, -4.34) * mm, "end": v(-78.07, -4.34) * mm});
            skLineSegment(sketch, "E584", {"start": v(-78.07, -4.34) * mm, "end": v(-78.09, -4.34) * mm});
            skLineSegment(sketch, "E585", {"start": v(-78.09, -4.34) * mm, "end": v(-78.14, -4.35) * mm});
            skLineSegment(sketch, "E586", {"start": v(-78.14, -4.35) * mm, "end": v(-78.25, -4.36) * mm});
            skLineSegment(sketch, "E587", {"start": v(-78.25, -4.36) * mm, "end": v(-78.47, -4.4) * mm});
            skLineSegment(sketch, "E588", {"start": v(-78.47, -4.4) * mm, "end": v(-78.96, -4.48) * mm});
            skLineSegment(sketch, "E589", {"start": v(-78.96, -4.48) * mm, "end": v(-80.02, -4.75) * mm});
            skLineSegment(sketch, "E590", {"start": v(-80.02, -4.75) * mm, "end": v(-82.25, -5.54) * mm});
            skArc(sketch, "E591", {"start": v(-82.25, -5.54) * mm, "mid": v(-82.15, -6.84) * mm, "end": v(-82.03, -8.14) * mm});
            skLineSegment(sketch, "E592", {"start": v(-77.7, -8.63) * mm, "end": v(-77.71, -8.63) * mm});
            skLineSegment(sketch, "E593", {"start": v(-77.71, -8.63) * mm, "end": v(-77.73, -8.63) * mm});
            skLineSegment(sketch, "E594", {"start": v(-77.73, -8.63) * mm, "end": v(-77.78, -8.64) * mm});
            skLineSegment(sketch, "E595", {"start": v(-77.78, -8.64) * mm, "end": v(-77.9, -8.64) * mm});
            skLineSegment(sketch, "E596", {"start": v(-77.9, -8.64) * mm, "end": v(-78.12, -8.65) * mm});
            skLineSegment(sketch, "E597", {"start": v(-78.12, -8.65) * mm, "end": v(-78.62, -8.64) * mm});
            skLineSegment(sketch, "E598", {"start": v(-78.62, -8.64) * mm, "end": v(-79.7, -8.55) * mm});
            skLineSegment(sketch, "E599", {"start": v(-79.7, -8.55) * mm, "end": v(-82.03, -8.14) * mm});
            skLineSegment(sketch, "E600", {"start": v(-75.94, -8.44) * mm, "end": v(-77.7, -8.63) * mm});
            skArc(sketch, "E601", {"start": v(-75.94, -8.44) * mm, "mid": v(-75.68, -10.53) * mm, "end": v(-75.36, -12.6) * mm});
            skLineSegment(sketch, "E602", {"start": v(-75.36, -12.6) * mm, "end": v(-77.1, -12.9) * mm});
            skLineSegment(sketch, "E603", {"start": v(-77.1, -12.9) * mm, "end": v(-77.12, -12.9) * mm});
            skLineSegment(sketch, "E604", {"start": v(-77.12, -12.9) * mm, "end": v(-77.14, -12.9) * mm});
            skLineSegment(sketch, "E605", {"start": v(-77.14, -12.9) * mm, "end": v(-77.19, -12.92) * mm});
            skLineSegment(sketch, "E606", {"start": v(-77.19, -12.92) * mm, "end": v(-77.3, -12.94) * mm});
            skLineSegment(sketch, "E607", {"start": v(-77.3, -12.94) * mm, "end": v(-77.52, -13) * mm});
            skLineSegment(sketch, "E608", {"start": v(-77.52, -13) * mm, "end": v(-78, -13.14) * mm});
            skLineSegment(sketch, "E609", {"start": v(-78, -13.14) * mm, "end": v(-79.01, -13.52) * mm});
            skLineSegment(sketch, "E610", {"start": v(-79.01, -13.52) * mm, "end": v(-81.14, -14.55) * mm});
            skArc(sketch, "E611", {"start": v(-81.14, -14.55) * mm, "mid": v(-80.9, -15.83) * mm, "end": v(-80.64, -17.12) * mm});
            skLineSegment(sketch, "E612", {"start": v(-76.28, -17.13) * mm, "end": v(-76.3, -17.13) * mm});
            skLineSegment(sketch, "E613", {"start": v(-76.3, -17.13) * mm, "end": v(-76.31, -17.13) * mm});
            skLineSegment(sketch, "E614", {"start": v(-76.31, -17.13) * mm, "end": v(-76.36, -17.14) * mm});
            skLineSegment(sketch, "E615", {"start": v(-76.36, -17.14) * mm, "end": v(-76.47, -17.16) * mm});
            skLineSegment(sketch, "E616", {"start": v(-76.47, -17.16) * mm, "end": v(-76.7, -17.2) * mm});
            skLineSegment(sketch, "E617", {"start": v(-76.7, -17.2) * mm, "end": v(-77.2, -17.24) * mm});
            skLineSegment(sketch, "E618", {"start": v(-77.2, -17.24) * mm, "end": v(-78.28, -17.27) * mm});
            skLineSegment(sketch, "E619", {"start": v(-78.28, -17.27) * mm, "end": v(-80.64, -17.12) * mm});
            skLineSegment(sketch, "E620", {"start": v(-74.55, -16.74) * mm, "end": v(-76.28, -17.13) * mm});
            skArc(sketch, "E621", {"start": v(-74.55, -16.74) * mm, "mid": v(-74.07, -18.79) * mm, "end": v(-73.52, -20.82) * mm});
            skLineSegment(sketch, "E622", {"start": v(-73.52, -20.82) * mm, "end": v(-75.22, -21.3) * mm});
            skLineSegment(sketch, "E623", {"start": v(-75.22, -21.3) * mm, "end": v(-75.24, -21.3) * mm});
            skLineSegment(sketch, "E624", {"start": v(-75.24, -21.3) * mm, "end": v(-75.25, -21.31) * mm});
            skLineSegment(sketch, "E625", {"start": v(-75.25, -21.31) * mm, "end": v(-75.3, -21.33) * mm});
            skLineSegment(sketch, "E626", {"start": v(-75.3, -21.33) * mm, "end": v(-75.4, -21.36) * mm});
            skLineSegment(sketch, "E627", {"start": v(-75.4, -21.36) * mm, "end": v(-75.62, -21.44) * mm});
            skLineSegment(sketch, "E628", {"start": v(-75.62, -21.44) * mm, "end": v(-76.08, -21.64) * mm});
            skLineSegment(sketch, "E629", {"start": v(-76.08, -21.64) * mm, "end": v(-77.05, -22.13) * mm});
            skLineSegment(sketch, "E630", {"start": v(-77.05, -22.13) * mm, "end": v(-79.05, -23.39) * mm});
            skArc(sketch, "E631", {"start": v(-79.05, -23.39) * mm, "mid": v(-78.67, -24.64) * mm, "end": v(-78.27, -25.88) * mm});
            skLineSegment(sketch, "E632", {"start": v(-73.94, -25.41) * mm, "end": v(-73.95, -25.42) * mm});
            skLineSegment(sketch, "E633", {"start": v(-73.95, -25.42) * mm, "end": v(-73.97, -25.42) * mm});
            skLineSegment(sketch, "E634", {"start": v(-73.97, -25.42) * mm, "end": v(-74.02, -25.44) * mm});
            skLineSegment(sketch, "E635", {"start": v(-74.02, -25.44) * mm, "end": v(-74.12, -25.47) * mm});
            skLineSegment(sketch, "E636", {"start": v(-74.12, -25.47) * mm, "end": v(-74.34, -25.52) * mm});
            skLineSegment(sketch, "E637", {"start": v(-74.34, -25.52) * mm, "end": v(-74.83, -25.62) * mm});
            skLineSegment(sketch, "E638", {"start": v(-74.83, -25.62) * mm, "end": v(-75.91, -25.77) * mm});
            skLineSegment(sketch, "E639", {"start": v(-75.91, -25.77) * mm, "end": v(-78.27, -25.88) * mm});
            skLineSegment(sketch, "E640", {"start": v(-72.26, -24.84) * mm, "end": v(-73.94, -25.41) * mm});
            skArc(sketch, "E641", {"start": v(-72.26, -24.84) * mm, "mid": v(-71.55, -26.82) * mm, "end": v(-70.79, -28.78) * mm});
            skLineSegment(sketch, "E642", {"start": v(-70.79, -28.78) * mm, "end": v(-72.43, -29.45) * mm});
            skLineSegment(sketch, "E643", {"start": v(-72.43, -29.45) * mm, "end": v(-72.44, -29.45) * mm});
            skLineSegment(sketch, "E644", {"start": v(-72.44, -29.45) * mm, "end": v(-72.46, -29.46) * mm});
            skLineSegment(sketch, "E645", {"start": v(-72.46, -29.46) * mm, "end": v(-72.5, -29.48) * mm});
            skLineSegment(sketch, "E646", {"start": v(-72.5, -29.48) * mm, "end": v(-72.6, -29.53) * mm});
            skLineSegment(sketch, "E647", {"start": v(-72.6, -29.53) * mm, "end": v(-72.8, -29.63) * mm});
            skLineSegment(sketch, "E648", {"start": v(-72.8, -29.63) * mm, "end": v(-73.24, -29.88) * mm});
            skLineSegment(sketch, "E649", {"start": v(-73.24, -29.88) * mm, "end": v(-74.15, -30.48) * mm});
            skLineSegment(sketch, "E650", {"start": v(-74.15, -30.48) * mm, "end": v(-76, -31.94) * mm});
            skArc(sketch, "E651", {"start": v(-76, -31.94) * mm, "mid": v(-75.49, -33.14) * mm, "end": v(-74.95, -34.34) * mm});
            skLineSegment(sketch, "E652", {"start": v(-70.7, -33.4) * mm, "end": v(-70.7, -33.4) * mm});
            skLineSegment(sketch, "E653", {"start": v(-70.7, -33.4) * mm, "end": v(-70.73, -33.4) * mm});
            skLineSegment(sketch, "E654", {"start": v(-70.73, -33.4) * mm, "end": v(-70.77, -33.43) * mm});
            skLineSegment(sketch, "E655", {"start": v(-70.77, -33.43) * mm, "end": v(-70.87, -33.47) * mm});
            skLineSegment(sketch, "E656", {"start": v(-70.87, -33.47) * mm, "end": v(-71.09, -33.55) * mm});
            skLineSegment(sketch, "E657", {"start": v(-71.09, -33.55) * mm, "end": v(-71.56, -33.7) * mm});
            skLineSegment(sketch, "E658", {"start": v(-71.56, -33.7) * mm, "end": v(-72.62, -33.97) * mm});
            skLineSegment(sketch, "E659", {"start": v(-72.62, -33.97) * mm, "end": v(-74.95, -34.34) * mm});
            skLineSegment(sketch, "E660", {"start": v(-69.1, -32.64) * mm, "end": v(-70.7, -33.4) * mm});
            skArc(sketch, "E661", {"start": v(-69.1, -32.64) * mm, "mid": v(-68.17, -34.53) * mm, "end": v(-67.2, -36.4) * mm});
            skLineSegment(sketch, "E662", {"start": v(-67.2, -36.4) * mm, "end": v(-68.75, -37.24) * mm});
            skLineSegment(sketch, "E663", {"start": v(-68.75, -37.24) * mm, "end": v(-68.76, -37.24) * mm});
            skLineSegment(sketch, "E664", {"start": v(-68.76, -37.24) * mm, "end": v(-68.78, -37.25) * mm});
            skLineSegment(sketch, "E665", {"start": v(-68.78, -37.25) * mm, "end": v(-68.82, -37.28) * mm});
            skLineSegment(sketch, "E666", {"start": v(-68.82, -37.28) * mm, "end": v(-68.92, -37.34) * mm});
            skLineSegment(sketch, "E667", {"start": v(-68.92, -37.34) * mm, "end": v(-69.1, -37.46) * mm});
            skLineSegment(sketch, "E668", {"start": v(-69.1, -37.46) * mm, "end": v(-69.51, -37.76) * mm});
            skLineSegment(sketch, "E669", {"start": v(-69.51, -37.76) * mm, "end": v(-70.35, -38.45) * mm});
            skLineSegment(sketch, "E670", {"start": v(-70.35, -38.45) * mm, "end": v(-72.03, -40.11) * mm});
            skArc(sketch, "E671", {"start": v(-72.03, -40.11) * mm, "mid": v(-71.39, -41.25) * mm, "end": v(-70.72, -42.37) * mm});
            skLineSegment(sketch, "E672", {"start": v(-66.6, -40.97) * mm, "end": v(-66.6, -40.98) * mm});
            skLineSegment(sketch, "E673", {"start": v(-66.6, -40.98) * mm, "end": v(-66.63, -40.99) * mm});
            skLineSegment(sketch, "E674", {"start": v(-66.63, -40.99) * mm, "end": v(-66.67, -41.01) * mm});
            skLineSegment(sketch, "E675", {"start": v(-66.67, -41.01) * mm, "end": v(-66.77, -41.06) * mm});
            skLineSegment(sketch, "E676", {"start": v(-66.77, -41.06) * mm, "end": v(-66.97, -41.16) * mm});
            skLineSegment(sketch, "E677", {"start": v(-66.97, -41.16) * mm, "end": v(-67.43, -41.37) * mm});
            skLineSegment(sketch, "E678", {"start": v(-67.43, -41.37) * mm, "end": v(-68.45, -41.75) * mm});
            skLineSegment(sketch, "E679", {"start": v(-68.45, -41.75) * mm, "end": v(-70.72, -42.37) * mm});
            skLineSegment(sketch, "E680", {"start": v(-65.1, -40.04) * mm, "end": v(-66.6, -40.97) * mm});
            skArc(sketch, "E681", {"start": v(-65.1, -40.04) * mm, "mid": v(-63.96, -41.82) * mm, "end": v(-62.79, -43.57) * mm});
            skLineSegment(sketch, "E682", {"start": v(-62.79, -43.57) * mm, "end": v(-64.24, -44.58) * mm});
            skLineSegment(sketch, "E683", {"start": v(-64.24, -44.58) * mm, "end": v(-64.25, -44.58) * mm});
            skLineSegment(sketch, "E684", {"start": v(-64.25, -44.58) * mm, "end": v(-64.27, -44.6) * mm});
            skLineSegment(sketch, "E685", {"start": v(-64.27, -44.6) * mm, "end": v(-64.3, -44.63) * mm});
            skLineSegment(sketch, "E686", {"start": v(-64.3, -44.63) * mm, "end": v(-64.4, -44.7) * mm});
            skLineSegment(sketch, "E687", {"start": v(-64.4, -44.7) * mm, "end": v(-64.57, -44.84) * mm});
            skLineSegment(sketch, "E688", {"start": v(-64.57, -44.84) * mm, "end": v(-64.94, -45.17) * mm});
            skLineSegment(sketch, "E689", {"start": v(-64.94, -45.17) * mm, "end": v(-65.7, -45.95) * mm});
            skLineSegment(sketch, "E690", {"start": v(-65.7, -45.95) * mm, "end": v(-67.19, -47.8) * mm});
            skArc(sketch, "E691", {"start": v(-67.19, -47.8) * mm, "mid": v(-66.42, -48.85) * mm, "end": v(-65.64, -49.9) * mm});
            skLineSegment(sketch, "E692", {"start": v(-61.7, -48.05) * mm, "end": v(-61.7, -48.05) * mm});
            skLineSegment(sketch, "E693", {"start": v(-61.7, -48.05) * mm, "end": v(-61.72, -48.07) * mm});
            skLineSegment(sketch, "E694", {"start": v(-61.72, -48.07) * mm, "end": v(-61.76, -48.1) * mm});
            skLineSegment(sketch, "E695", {"start": v(-61.76, -48.1) * mm, "end": v(-61.85, -48.16) * mm});
            skLineSegment(sketch, "E696", {"start": v(-61.85, -48.16) * mm, "end": v(-62.04, -48.28) * mm});
            skLineSegment(sketch, "E697", {"start": v(-62.04, -48.28) * mm, "end": v(-62.47, -48.54) * mm});
            skLineSegment(sketch, "E698", {"start": v(-62.47, -48.54) * mm, "end": v(-63.44, -49.03) * mm});
            skLineSegment(sketch, "E699", {"start": v(-63.44, -49.03) * mm, "end": v(-65.64, -49.9) * mm});
            skLineSegment(sketch, "E700", {"start": v(-60.3, -46.96) * mm, "end": v(-61.7, -48.05) * mm});
            skArc(sketch, "E701", {"start": v(-60.3, -46.96) * mm, "mid": v(-58.98, -48.6) * mm, "end": v(-57.62, -50.21) * mm});
            skLineSegment(sketch, "E702", {"start": v(-57.62, -50.21) * mm, "end": v(-58.95, -51.37) * mm});
            skLineSegment(sketch, "E703", {"start": v(-58.95, -51.37) * mm, "end": v(-58.96, -51.38) * mm});
            skLineSegment(sketch, "E704", {"start": v(-58.96, -51.38) * mm, "end": v(-58.97, -51.4) * mm});
            skLineSegment(sketch, "E705", {"start": v(-58.97, -51.4) * mm, "end": v(-59.01, -51.43) * mm});
            skLineSegment(sketch, "E706", {"start": v(-59.01, -51.43) * mm, "end": v(-59.1, -51.5) * mm});
            skLineSegment(sketch, "E707", {"start": v(-59.1, -51.5) * mm, "end": v(-59.25, -51.67) * mm});
            skLineSegment(sketch, "E708", {"start": v(-59.25, -51.67) * mm, "end": v(-59.58, -52.04) * mm});
            skLineSegment(sketch, "E709", {"start": v(-59.58, -52.04) * mm, "end": v(-60.25, -52.9) * mm});
            skLineSegment(sketch, "E710", {"start": v(-60.25, -52.9) * mm, "end": v(-61.52, -54.9) * mm});
            skArc(sketch, "E711", {"start": v(-61.52, -54.9) * mm, "mid": v(-60.65, -55.86) * mm, "end": v(-59.75, -56.82) * mm});
            skLineSegment(sketch, "E712", {"start": v(-56.03, -54.54) * mm, "end": v(-56.04, -54.55) * mm});
            skLineSegment(sketch, "E713", {"start": v(-56.04, -54.55) * mm, "end": v(-56.06, -54.56) * mm});
            skLineSegment(sketch, "E714", {"start": v(-56.06, -54.56) * mm, "end": v(-56.1, -54.6) * mm});
            skLineSegment(sketch, "E715", {"start": v(-56.1, -54.6) * mm, "end": v(-56.18, -54.67) * mm});
            skLineSegment(sketch, "E716", {"start": v(-56.18, -54.67) * mm, "end": v(-56.35, -54.81) * mm});
            skLineSegment(sketch, "E717", {"start": v(-56.35, -54.81) * mm, "end": v(-56.76, -55.11) * mm});
            skLineSegment(sketch, "E718", {"start": v(-56.76, -55.11) * mm, "end": v(-57.67, -55.7) * mm});
            skLineSegment(sketch, "E719", {"start": v(-57.67, -55.7) * mm, "end": v(-59.75, -56.82) * mm});
            skLineSegment(sketch, "E720", {"start": v(-54.77, -53.3) * mm, "end": v(-56.03, -54.54) * mm});
            skArc(sketch, "E721", {"start": v(-54.77, -53.3) * mm, "mid": v(-53.28, -54.8) * mm, "end": v(-51.75, -56.24) * mm});
            skLineSegment(sketch, "E722", {"start": v(-51.75, -56.24) * mm, "end": v(-52.95, -57.55) * mm});
            skLineSegment(sketch, "E723", {"start": v(-52.95, -57.55) * mm, "end": v(-52.95, -57.55) * mm});
            skLineSegment(sketch, "E724", {"start": v(-52.95, -57.55) * mm, "end": v(-52.97, -57.57) * mm});
            skLineSegment(sketch, "E725", {"start": v(-52.97, -57.57) * mm, "end": v(-53, -57.6) * mm});
            skLineSegment(sketch, "E726", {"start": v(-53, -57.6) * mm, "end": v(-53.07, -57.7) * mm});
            skLineSegment(sketch, "E727", {"start": v(-53.07, -57.7) * mm, "end": v(-53.2, -57.87) * mm});
            skLineSegment(sketch, "E728", {"start": v(-53.2, -57.87) * mm, "end": v(-53.5, -58.28) * mm});
            skLineSegment(sketch, "E729", {"start": v(-53.5, -58.28) * mm, "end": v(-54.07, -59.21) * mm});
            skLineSegment(sketch, "E730", {"start": v(-54.07, -59.21) * mm, "end": v(-55.12, -61.33) * mm});
            skArc(sketch, "E731", {"start": v(-55.12, -61.33) * mm, "mid": v(-54.14, -62.2) * mm, "end": v(-53.14, -63.04) * mm});
            skLineSegment(sketch, "E732", {"start": v(-49.7, -60.38) * mm, "end": v(-49.7, -60.38) * mm});
            skLineSegment(sketch, "E733", {"start": v(-49.7, -60.38) * mm, "end": v(-49.72, -60.4) * mm});
            skLineSegment(sketch, "E734", {"start": v(-49.72, -60.4) * mm, "end": v(-49.75, -60.44) * mm});
            skLineSegment(sketch, "E735", {"start": v(-49.75, -60.44) * mm, "end": v(-49.83, -60.52) * mm});
            skLineSegment(sketch, "E736", {"start": v(-49.83, -60.52) * mm, "end": v(-49.99, -60.68) * mm});
            skLineSegment(sketch, "E737", {"start": v(-49.99, -60.68) * mm, "end": v(-50.35, -61.02) * mm});
            skLineSegment(sketch, "E738", {"start": v(-50.35, -61.02) * mm, "end": v(-51.2, -61.71) * mm});
            skLineSegment(sketch, "E739", {"start": v(-51.2, -61.71) * mm, "end": v(-53.14, -63.04) * mm});
            skLineSegment(sketch, "E740", {"start": v(-48.57, -59) * mm, "end": v(-49.7, -60.38) * mm});
            skArc(sketch, "E741", {"start": v(-48.57, -59) * mm, "mid": v(-46.93, -60.33) * mm, "end": v(-45.25, -61.6) * mm});
            skLineSegment(sketch, "E742", {"start": v(-45.25, -61.6) * mm, "end": v(-46.3, -63.02) * mm});
            skLineSegment(sketch, "E743", {"start": v(-46.3, -63.02) * mm, "end": v(-46.3, -63.03) * mm});
            skLineSegment(sketch, "E744", {"start": v(-46.3, -63.03) * mm, "end": v(-46.32, -63.05) * mm});
            skLineSegment(sketch, "E745", {"start": v(-46.32, -63.05) * mm, "end": v(-46.34, -63.1) * mm});
            skLineSegment(sketch, "E746", {"start": v(-46.34, -63.1) * mm, "end": v(-46.4, -63.18) * mm});
            skLineSegment(sketch, "E747", {"start": v(-46.4, -63.18) * mm, "end": v(-46.52, -63.38) * mm});
            skLineSegment(sketch, "E748", {"start": v(-46.52, -63.38) * mm, "end": v(-46.76, -63.81) * mm});
            skLineSegment(sketch, "E749", {"start": v(-46.76, -63.81) * mm, "end": v(-47.23, -64.8) * mm});
            skLineSegment(sketch, "E750", {"start": v(-47.23, -64.8) * mm, "end": v(-48.04, -67.02) * mm});
            skArc(sketch, "E751", {"start": v(-48.04, -67.02) * mm, "mid": v(-46.97, -67.77) * mm, "end": v(-45.89, -68.5) * mm});
            skLineSegment(sketch, "E752", {"start": v(-42.76, -65.48) * mm, "end": v(-42.76, -65.49) * mm});
            skLineSegment(sketch, "E753", {"start": v(-42.76, -65.49) * mm, "end": v(-42.78, -65.5) * mm});
            skLineSegment(sketch, "E754", {"start": v(-42.78, -65.5) * mm, "end": v(-42.8, -65.54) * mm});
            skLineSegment(sketch, "E755", {"start": v(-42.8, -65.54) * mm, "end": v(-42.87, -65.63) * mm});
            skLineSegment(sketch, "E756", {"start": v(-42.87, -65.63) * mm, "end": v(-43, -65.81) * mm});
            skLineSegment(sketch, "E757", {"start": v(-43, -65.81) * mm, "end": v(-43.34, -66.2) * mm});
            skLineSegment(sketch, "E758", {"start": v(-43.34, -66.2) * mm, "end": v(-44.1, -66.97) * mm});
            skLineSegment(sketch, "E759", {"start": v(-44.1, -66.97) * mm, "end": v(-45.89, -68.5) * mm});
            skLineSegment(sketch, "E760", {"start": v(-41.79, -64) * mm, "end": v(-42.76, -65.48) * mm});
            skArc(sketch, "E761", {"start": v(-41.79, -64) * mm, "mid": v(-40.01, -65.12) * mm, "end": v(-38.2, -66.2) * mm});
            skLineSegment(sketch, "E762", {"start": v(-38.2, -66.2) * mm, "end": v(-39.09, -67.73) * mm});
            skLineSegment(sketch, "E763", {"start": v(-39.09, -67.73) * mm, "end": v(-39.1, -67.74) * mm});
            skLineSegment(sketch, "E764", {"start": v(-39.1, -67.74) * mm, "end": v(-39.1, -67.76) * mm});
            skLineSegment(sketch, "E765", {"start": v(-39.1, -67.76) * mm, "end": v(-39.13, -67.8) * mm});
            skLineSegment(sketch, "E766", {"start": v(-39.13, -67.8) * mm, "end": v(-39.18, -67.9) * mm});
            skLineSegment(sketch, "E767", {"start": v(-39.18, -67.9) * mm, "end": v(-39.27, -68.1) * mm});
            skLineSegment(sketch, "E768", {"start": v(-39.27, -68.1) * mm, "end": v(-39.46, -68.57) * mm});
            skLineSegment(sketch, "E769", {"start": v(-39.46, -68.57) * mm, "end": v(-39.82, -69.6) * mm});
            skLineSegment(sketch, "E770", {"start": v(-39.82, -69.6) * mm, "end": v(-40.38, -71.9) * mm});
            skArc(sketch, "E771", {"start": v(-40.38, -71.9) * mm, "mid": v(-39.23, -72.53) * mm, "end": v(-38.08, -73.14) * mm});
            skLineSegment(sketch, "E772", {"start": v(-35.3, -69.78) * mm, "end": v(-35.3, -69.8) * mm});
            skLineSegment(sketch, "E773", {"start": v(-35.3, -69.8) * mm, "end": v(-35.31, -69.81) * mm});
            skLineSegment(sketch, "E774", {"start": v(-35.31, -69.81) * mm, "end": v(-35.34, -69.86) * mm});
            skLineSegment(sketch, "E775", {"start": v(-35.34, -69.86) * mm, "end": v(-35.4, -69.95) * mm});
            skLineSegment(sketch, "E776", {"start": v(-35.4, -69.95) * mm, "end": v(-35.51, -70.14) * mm});
            skLineSegment(sketch, "E777", {"start": v(-35.51, -70.14) * mm, "end": v(-35.8, -70.56) * mm});
            skLineSegment(sketch, "E778", {"start": v(-35.8, -70.56) * mm, "end": v(-36.46, -71.42) * mm});
            skLineSegment(sketch, "E779", {"start": v(-36.46, -71.42) * mm, "end": v(-38.08, -73.14) * mm});
            skLineSegment(sketch, "E780", {"start": v(-34.5, -68.2) * mm, "end": v(-35.3, -69.78) * mm});
            skArc(sketch, "E781", {"start": v(-34.5, -68.2) * mm, "mid": v(-32.6, -69.13) * mm, "end": v(-30.7, -70) * mm});
            skLineSegment(sketch, "E782", {"start": v(-30.7, -70) * mm, "end": v(-31.4, -71.62) * mm});
            skLineSegment(sketch, "E783", {"start": v(-31.4, -71.62) * mm, "end": v(-31.4, -71.63) * mm});
            skLineSegment(sketch, "E784", {"start": v(-31.4, -71.63) * mm, "end": v(-31.41, -71.65) * mm});
            skLineSegment(sketch, "E785", {"start": v(-31.41, -71.65) * mm, "end": v(-31.43, -71.7) * mm});
            skLineSegment(sketch, "E786", {"start": v(-31.43, -71.7) * mm, "end": v(-31.47, -71.8) * mm});
            skLineSegment(sketch, "E787", {"start": v(-31.47, -71.8) * mm, "end": v(-31.54, -72.02) * mm});
            skLineSegment(sketch, "E788", {"start": v(-31.54, -72.02) * mm, "end": v(-31.68, -72.5) * mm});
            skLineSegment(sketch, "E789", {"start": v(-31.68, -72.5) * mm, "end": v(-31.92, -73.56) * mm});
            skLineSegment(sketch, "E790", {"start": v(-31.92, -73.56) * mm, "end": v(-32.23, -75.9) * mm});
            skArc(sketch, "E791", {"start": v(-32.23, -75.9) * mm, "mid": v(-31.02, -76.4) * mm, "end": v(-29.8, -76.89) * mm});
            skLineSegment(sketch, "E792", {"start": v(-27.41, -73.24) * mm, "end": v(-27.42, -73.25) * mm});
            skLineSegment(sketch, "E793", {"start": v(-27.42, -73.25) * mm, "end": v(-27.42, -73.27) * mm});
            skLineSegment(sketch, "E794", {"start": v(-27.42, -73.27) * mm, "end": v(-27.44, -73.32) * mm});
            skLineSegment(sketch, "E795", {"start": v(-27.44, -73.32) * mm, "end": v(-27.49, -73.42) * mm});
            skLineSegment(sketch, "E796", {"start": v(-27.49, -73.42) * mm, "end": v(-27.58, -73.62) * mm});
            skLineSegment(sketch, "E797", {"start": v(-27.58, -73.62) * mm, "end": v(-27.82, -74.07) * mm});
            skLineSegment(sketch, "E798", {"start": v(-27.82, -74.07) * mm, "end": v(-28.39, -75) * mm});
            skLineSegment(sketch, "E799", {"start": v(-28.39, -75) * mm, "end": v(-29.8, -76.89) * mm});
            skLineSegment(sketch, "E800", {"start": v(-26.8, -71.58) * mm, "end": v(-27.41, -73.24) * mm});
            skArc(sketch, "E801", {"start": v(-26.8, -71.58) * mm, "mid": v(-24.8, -72.3) * mm, "end": v(-22.8, -72.95) * mm});
            skLineSegment(sketch, "E802", {"start": v(-22.8, -72.95) * mm, "end": v(-23.34, -74.64) * mm});
            skLineSegment(sketch, "E803", {"start": v(-23.34, -74.64) * mm, "end": v(-23.34, -74.65) * mm});
            skLineSegment(sketch, "E804", {"start": v(-23.34, -74.65) * mm, "end": v(-23.34, -74.67) * mm});
            skLineSegment(sketch, "E805", {"start": v(-23.34, -74.67) * mm, "end": v(-23.36, -74.72) * mm});
            skLineSegment(sketch, "E806", {"start": v(-23.36, -74.72) * mm, "end": v(-23.39, -74.83) * mm});
            skLineSegment(sketch, "E807", {"start": v(-23.39, -74.83) * mm, "end": v(-23.43, -75.05) * mm});
            skLineSegment(sketch, "E808", {"start": v(-23.43, -75.05) * mm, "end": v(-23.52, -75.54) * mm});
            skLineSegment(sketch, "E809", {"start": v(-23.52, -75.54) * mm, "end": v(-23.64, -76.62) * mm});
            skLineSegment(sketch, "E810", {"start": v(-23.64, -76.62) * mm, "end": v(-23.68, -78.99) * mm});
            skArc(sketch, "E811", {"start": v(-23.68, -78.99) * mm, "mid": v(-22.43, -79.35) * mm, "end": v(-21.17, -79.7) * mm});
            skLineSegment(sketch, "E812", {"start": v(-19.2, -75.81) * mm, "end": v(-19.2, -75.82) * mm});
            skLineSegment(sketch, "E813", {"start": v(-19.2, -75.82) * mm, "end": v(-19.2, -75.84) * mm});
            skLineSegment(sketch, "E814", {"start": v(-19.2, -75.84) * mm, "end": v(-19.21, -75.9) * mm});
            skLineSegment(sketch, "E815", {"start": v(-19.21, -75.9) * mm, "end": v(-19.25, -76) * mm});
            skLineSegment(sketch, "E816", {"start": v(-19.25, -76) * mm, "end": v(-19.32, -76.21) * mm});
            skLineSegment(sketch, "E817", {"start": v(-19.32, -76.21) * mm, "end": v(-19.5, -76.68) * mm});
            skLineSegment(sketch, "E818", {"start": v(-19.5, -76.68) * mm, "end": v(-19.97, -77.66) * mm});
            skLineSegment(sketch, "E819", {"start": v(-19.97, -77.66) * mm, "end": v(-21.17, -79.7) * mm});
            skLineSegment(sketch, "E820", {"start": v(-18.76, -74.1) * mm, "end": v(-19.2, -75.81) * mm});
            skArc(sketch, "E821", {"start": v(-18.76, -74.1) * mm, "mid": v(-16.7, -74.59) * mm, "end": v(-14.65, -75.02) * mm});
            skLineSegment(sketch, "E822", {"start": v(-14.65, -75.02) * mm, "end": v(-14.99, -76.76) * mm});
            skLineSegment(sketch, "E823", {"start": v(-14.99, -76.76) * mm, "end": v(-14.99, -76.77) * mm});
            skLineSegment(sketch, "E824", {"start": v(-14.99, -76.77) * mm, "end": v(-15, -76.79) * mm});
            skLineSegment(sketch, "E825", {"start": v(-15, -76.79) * mm, "end": v(-15, -76.84) * mm});
            skLineSegment(sketch, "E826", {"start": v(-15, -76.84) * mm, "end": v(-15.02, -76.95) * mm});
            skLineSegment(sketch, "E827", {"start": v(-15.02, -76.95) * mm, "end": v(-15.04, -77.17) * mm});
            skLineSegment(sketch, "E828", {"start": v(-15.04, -77.17) * mm, "end": v(-15.07, -77.67) * mm});
            skLineSegment(sketch, "E829", {"start": v(-15.07, -77.67) * mm, "end": v(-15.07, -78.76) * mm});
            skLineSegment(sketch, "E830", {"start": v(-15.07, -78.76) * mm, "end": v(-14.86, -81.11) * mm});
            skArc(sketch, "E831", {"start": v(-14.86, -81.11) * mm, "mid": v(-13.57, -81.34) * mm, "end": v(-12.28, -81.54) * mm});
            skLineSegment(sketch, "E832", {"start": v(-10.74, -77.46) * mm, "end": v(-10.74, -77.48) * mm});
            skLineSegment(sketch, "E833", {"start": v(-10.74, -77.48) * mm, "end": v(-10.74, -77.5) * mm});
            skLineSegment(sketch, "E834", {"start": v(-10.74, -77.5) * mm, "end": v(-10.75, -77.55) * mm});
            skLineSegment(sketch, "E835", {"start": v(-10.75, -77.55) * mm, "end": v(-10.77, -77.65) * mm});
            skLineSegment(sketch, "E836", {"start": v(-10.77, -77.65) * mm, "end": v(-10.82, -77.87) * mm});
            skLineSegment(sketch, "E837", {"start": v(-10.82, -77.87) * mm, "end": v(-10.96, -78.36) * mm});
            skLineSegment(sketch, "E838", {"start": v(-10.96, -78.36) * mm, "end": v(-11.3, -79.39) * mm});
            skLineSegment(sketch, "E839", {"start": v(-11.3, -79.39) * mm, "end": v(-12.28, -81.54) * mm});
            skLineSegment(sketch, "E840", {"start": v(-10.5, -75.71) * mm, "end": v(-10.74, -77.46) * mm});
            skArc(sketch, "E841", {"start": v(-10.5, -75.71) * mm, "mid": v(-8.4, -75.97) * mm, "end": v(-6.3, -76.17) * mm});
            skLineSegment(sketch, "E842", {"start": v(-6.3, -76.17) * mm, "end": v(-6.46, -77.94) * mm});
            skLineSegment(sketch, "E843", {"start": v(-6.46, -77.94) * mm, "end": v(-6.46, -77.95) * mm});
            skLineSegment(sketch, "E844", {"start": v(-6.46, -77.95) * mm, "end": v(-6.46, -77.97) * mm});
            skLineSegment(sketch, "E845", {"start": v(-6.46, -77.97) * mm, "end": v(-6.46, -78.02) * mm});
            skLineSegment(sketch, "E846", {"start": v(-6.46, -78.02) * mm, "end": v(-6.46, -78.13) * mm});
            skLineSegment(sketch, "E847", {"start": v(-6.46, -78.13) * mm, "end": v(-6.46, -78.36) * mm});
            skLineSegment(sketch, "E848", {"start": v(-6.46, -78.36) * mm, "end": v(-6.44, -78.86) * mm});
            skLineSegment(sketch, "E849", {"start": v(-6.44, -78.86) * mm, "end": v(-6.32, -79.94) * mm});
            skLineSegment(sketch, "E850", {"start": v(-6.32, -79.94) * mm, "end": v(-5.85, -82.26) * mm});
            skArc(sketch, "E851", {"start": v(-5.85, -82.26) * mm, "mid": v(-4.54, -82.34) * mm, "end": v(-3.24, -82.4) * mm});
            skLineSegment(sketch, "E852", {"start": v(-2.15, -78.18) * mm, "end": v(-2.15, -78.19) * mm});
            skLineSegment(sketch, "E853", {"start": v(-2.15, -78.19) * mm, "end": v(-2.16, -78.2) * mm});
            skLineSegment(sketch, "E854", {"start": v(-2.16, -78.2) * mm, "end": v(-2.16, -78.26) * mm});
            skLineSegment(sketch, "E855", {"start": v(-2.16, -78.26) * mm, "end": v(-2.17, -78.37) * mm});
            skLineSegment(sketch, "E856", {"start": v(-2.17, -78.37) * mm, "end": v(-2.2, -78.6) * mm});
            skLineSegment(sketch, "E857", {"start": v(-2.2, -78.6) * mm, "end": v(-2.27, -79.09) * mm});
            skLineSegment(sketch, "E858", {"start": v(-2.27, -79.09) * mm, "end": v(-2.51, -80.15) * mm});
            skLineSegment(sketch, "E859", {"start": v(-2.51, -80.15) * mm, "end": v(-3.24, -82.4) * mm});
            skLineSegment(sketch, "E860", {"start": v(-2.1, -76.4) * mm, "end": v(-2.15, -78.18) * mm});
            skArc(sketch, "E861", {"start": v(-2.1, -76.4) * mm, "mid": v(0, -76.44) * mm, "end": v(2.1, -76.4) * mm});
            skLineSegment(sketch, "E862", {"start": v(2.1, -76.4) * mm, "end": v(2.15, -78.18) * mm});
            skLineSegment(sketch, "E863", {"start": v(2.15, -78.18) * mm, "end": v(2.15, -78.19) * mm});
            skLineSegment(sketch, "E864", {"start": v(2.15, -78.19) * mm, "end": v(2.16, -78.2) * mm});
            skLineSegment(sketch, "E865", {"start": v(2.16, -78.2) * mm, "end": v(2.16, -78.26) * mm});
            skLineSegment(sketch, "E866", {"start": v(2.16, -78.26) * mm, "end": v(2.17, -78.37) * mm});
            skLineSegment(sketch, "E867", {"start": v(2.17, -78.37) * mm, "end": v(2.2, -78.6) * mm});
            skLineSegment(sketch, "E868", {"start": v(2.2, -78.6) * mm, "end": v(2.27, -79.09) * mm});
            skLineSegment(sketch, "E869", {"start": v(2.27, -79.09) * mm, "end": v(2.51, -80.15) * mm});
            skLineSegment(sketch, "E870", {"start": v(2.51, -80.15) * mm, "end": v(3.24, -82.4) * mm});
            skArc(sketch, "E871", {"start": v(3.24, -82.4) * mm, "mid": v(4.54, -82.34) * mm, "end": v(5.85, -82.26) * mm});
            skLineSegment(sketch, "E872", {"start": v(6.46, -77.94) * mm, "end": v(6.46, -77.95) * mm});
            skLineSegment(sketch, "E873", {"start": v(6.46, -77.95) * mm, "end": v(6.46, -77.97) * mm});
            skLineSegment(sketch, "E874", {"start": v(6.46, -77.97) * mm, "end": v(6.46, -78.02) * mm});
            skLineSegment(sketch, "E875", {"start": v(6.46, -78.02) * mm, "end": v(6.46, -78.13) * mm});
            skLineSegment(sketch, "E876", {"start": v(6.46, -78.13) * mm, "end": v(6.46, -78.36) * mm});
            skLineSegment(sketch, "E877", {"start": v(6.46, -78.36) * mm, "end": v(6.44, -78.86) * mm});
            skLineSegment(sketch, "E878", {"start": v(6.44, -78.86) * mm, "end": v(6.32, -79.94) * mm});
            skLineSegment(sketch, "E879", {"start": v(6.32, -79.94) * mm, "end": v(5.85, -82.26) * mm});
            skLineSegment(sketch, "E880", {"start": v(6.3, -76.17) * mm, "end": v(6.46, -77.94) * mm});
            skArc(sketch, "E881", {"start": v(6.3, -76.17) * mm, "mid": v(8.4, -75.97) * mm, "end": v(10.5, -75.71) * mm});
            skLineSegment(sketch, "E882", {"start": v(10.5, -75.71) * mm, "end": v(10.74, -77.46) * mm});
            skLineSegment(sketch, "E883", {"start": v(10.74, -77.46) * mm, "end": v(10.74, -77.48) * mm});
            skLineSegment(sketch, "E884", {"start": v(10.74, -77.48) * mm, "end": v(10.74, -77.5) * mm});
            skLineSegment(sketch, "E885", {"start": v(10.74, -77.5) * mm, "end": v(10.75, -77.55) * mm});
            skLineSegment(sketch, "E886", {"start": v(10.75, -77.55) * mm, "end": v(10.77, -77.65) * mm});
            skLineSegment(sketch, "E887", {"start": v(10.77, -77.65) * mm, "end": v(10.82, -77.87) * mm});
            skLineSegment(sketch, "E888", {"start": v(10.82, -77.87) * mm, "end": v(10.96, -78.36) * mm});
            skLineSegment(sketch, "E889", {"start": v(10.96, -78.36) * mm, "end": v(11.3, -79.39) * mm});
            skLineSegment(sketch, "E890", {"start": v(11.3, -79.39) * mm, "end": v(12.28, -81.54) * mm});
            skArc(sketch, "E891", {"start": v(12.28, -81.54) * mm, "mid": v(13.57, -81.34) * mm, "end": v(14.86, -81.11) * mm});
            skLineSegment(sketch, "E892", {"start": v(14.99, -76.76) * mm, "end": v(14.99, -76.77) * mm});
            skLineSegment(sketch, "E893", {"start": v(14.99, -76.77) * mm, "end": v(15, -76.79) * mm});
            skLineSegment(sketch, "E894", {"start": v(15, -76.79) * mm, "end": v(15, -76.84) * mm});
            skLineSegment(sketch, "E895", {"start": v(15, -76.84) * mm, "end": v(15.02, -76.95) * mm});
            skLineSegment(sketch, "E896", {"start": v(15.02, -76.95) * mm, "end": v(15.04, -77.17) * mm});
            skLineSegment(sketch, "E897", {"start": v(15.04, -77.17) * mm, "end": v(15.07, -77.67) * mm});
            skLineSegment(sketch, "E898", {"start": v(15.07, -77.67) * mm, "end": v(15.07, -78.76) * mm});
            skLineSegment(sketch, "E899", {"start": v(15.07, -78.76) * mm, "end": v(14.86, -81.11) * mm});
            skLineSegment(sketch, "E900", {"start": v(14.65, -75.02) * mm, "end": v(14.99, -76.76) * mm});
            skArc(sketch, "E901", {"start": v(14.65, -75.02) * mm, "mid": v(16.7, -74.59) * mm, "end": v(18.76, -74.1) * mm});
            skLineSegment(sketch, "E902", {"start": v(18.76, -74.1) * mm, "end": v(19.2, -75.81) * mm});
            skLineSegment(sketch, "E903", {"start": v(19.2, -75.81) * mm, "end": v(19.2, -75.82) * mm});
            skLineSegment(sketch, "E904", {"start": v(19.2, -75.82) * mm, "end": v(19.2, -75.84) * mm});
            skLineSegment(sketch, "E905", {"start": v(19.2, -75.84) * mm, "end": v(19.21, -75.9) * mm});
            skLineSegment(sketch, "E906", {"start": v(19.21, -75.9) * mm, "end": v(19.25, -76) * mm});
            skLineSegment(sketch, "E907", {"start": v(19.25, -76) * mm, "end": v(19.32, -76.21) * mm});
            skLineSegment(sketch, "E908", {"start": v(19.32, -76.21) * mm, "end": v(19.5, -76.68) * mm});
            skLineSegment(sketch, "E909", {"start": v(19.5, -76.68) * mm, "end": v(19.97, -77.66) * mm});
            skLineSegment(sketch, "E910", {"start": v(19.97, -77.66) * mm, "end": v(21.17, -79.7) * mm});
            skArc(sketch, "E911", {"start": v(21.17, -79.7) * mm, "mid": v(22.43, -79.35) * mm, "end": v(23.68, -78.99) * mm});
            skLineSegment(sketch, "E912", {"start": v(23.34, -74.64) * mm, "end": v(23.34, -74.65) * mm});
            skLineSegment(sketch, "E913", {"start": v(23.34, -74.65) * mm, "end": v(23.34, -74.67) * mm});
            skLineSegment(sketch, "E914", {"start": v(23.34, -74.67) * mm, "end": v(23.36, -74.72) * mm});
            skLineSegment(sketch, "E915", {"start": v(23.36, -74.72) * mm, "end": v(23.39, -74.83) * mm});
            skLineSegment(sketch, "E916", {"start": v(23.39, -74.83) * mm, "end": v(23.43, -75.05) * mm});
            skLineSegment(sketch, "E917", {"start": v(23.43, -75.05) * mm, "end": v(23.52, -75.54) * mm});
            skLineSegment(sketch, "E918", {"start": v(23.52, -75.54) * mm, "end": v(23.64, -76.62) * mm});
            skLineSegment(sketch, "E919", {"start": v(23.64, -76.62) * mm, "end": v(23.68, -78.99) * mm});
            skLineSegment(sketch, "E920", {"start": v(22.8, -72.95) * mm, "end": v(23.34, -74.64) * mm});
            skArc(sketch, "E921", {"start": v(22.8, -72.95) * mm, "mid": v(24.8, -72.3) * mm, "end": v(26.8, -71.58) * mm});
            skLineSegment(sketch, "E922", {"start": v(26.8, -71.58) * mm, "end": v(27.41, -73.24) * mm});
            skLineSegment(sketch, "E923", {"start": v(27.41, -73.24) * mm, "end": v(27.42, -73.25) * mm});
            skLineSegment(sketch, "E924", {"start": v(27.42, -73.25) * mm, "end": v(27.42, -73.27) * mm});
            skLineSegment(sketch, "E925", {"start": v(27.42, -73.27) * mm, "end": v(27.44, -73.32) * mm});
            skLineSegment(sketch, "E926", {"start": v(27.44, -73.32) * mm, "end": v(27.49, -73.42) * mm});
            skLineSegment(sketch, "E927", {"start": v(27.49, -73.42) * mm, "end": v(27.58, -73.62) * mm});
            skLineSegment(sketch, "E928", {"start": v(27.58, -73.62) * mm, "end": v(27.82, -74.07) * mm});
            skLineSegment(sketch, "E929", {"start": v(27.82, -74.07) * mm, "end": v(28.39, -75) * mm});
            skLineSegment(sketch, "E930", {"start": v(28.39, -75) * mm, "end": v(29.8, -76.89) * mm});
            skArc(sketch, "E931", {"start": v(29.8, -76.89) * mm, "mid": v(31.02, -76.4) * mm, "end": v(32.23, -75.9) * mm});
            skLineSegment(sketch, "E932", {"start": v(31.4, -71.62) * mm, "end": v(31.4, -71.63) * mm});
            skLineSegment(sketch, "E933", {"start": v(31.4, -71.63) * mm, "end": v(31.41, -71.65) * mm});
            skLineSegment(sketch, "E934", {"start": v(31.41, -71.65) * mm, "end": v(31.43, -71.7) * mm});
            skLineSegment(sketch, "E935", {"start": v(31.43, -71.7) * mm, "end": v(31.47, -71.8) * mm});
            skLineSegment(sketch, "E936", {"start": v(31.47, -71.8) * mm, "end": v(31.54, -72.02) * mm});
            skLineSegment(sketch, "E937", {"start": v(31.54, -72.02) * mm, "end": v(31.68, -72.5) * mm});
            skLineSegment(sketch, "E938", {"start": v(31.68, -72.5) * mm, "end": v(31.92, -73.56) * mm});
            skLineSegment(sketch, "E939", {"start": v(31.92, -73.56) * mm, "end": v(32.23, -75.9) * mm});
            skLineSegment(sketch, "E940", {"start": v(30.7, -70) * mm, "end": v(31.4, -71.62) * mm});
            skArc(sketch, "E941", {"start": v(30.7, -70) * mm, "mid": v(32.6, -69.13) * mm, "end": v(34.5, -68.2) * mm});
            skLineSegment(sketch, "E942", {"start": v(34.5, -68.2) * mm, "end": v(35.3, -69.78) * mm});
            skLineSegment(sketch, "E943", {"start": v(35.3, -69.78) * mm, "end": v(35.3, -69.8) * mm});
            skLineSegment(sketch, "E944", {"start": v(35.3, -69.8) * mm, "end": v(35.31, -69.81) * mm});
            skLineSegment(sketch, "E945", {"start": v(35.31, -69.81) * mm, "end": v(35.34, -69.86) * mm});
            skLineSegment(sketch, "E946", {"start": v(35.34, -69.86) * mm, "end": v(35.4, -69.95) * mm});
            skLineSegment(sketch, "E947", {"start": v(35.4, -69.95) * mm, "end": v(35.51, -70.14) * mm});
            skLineSegment(sketch, "E948", {"start": v(35.51, -70.14) * mm, "end": v(35.8, -70.56) * mm});
            skLineSegment(sketch, "E949", {"start": v(35.8, -70.56) * mm, "end": v(36.46, -71.42) * mm});
            skLineSegment(sketch, "E950", {"start": v(36.46, -71.42) * mm, "end": v(38.08, -73.14) * mm});
            skArc(sketch, "E951", {"start": v(38.08, -73.14) * mm, "mid": v(39.23, -72.53) * mm, "end": v(40.38, -71.9) * mm});
            skLineSegment(sketch, "E952", {"start": v(39.09, -67.73) * mm, "end": v(39.1, -67.74) * mm});
            skLineSegment(sketch, "E953", {"start": v(39.1, -67.74) * mm, "end": v(39.1, -67.76) * mm});
            skLineSegment(sketch, "E954", {"start": v(39.1, -67.76) * mm, "end": v(39.13, -67.8) * mm});
            skLineSegment(sketch, "E955", {"start": v(39.13, -67.8) * mm, "end": v(39.18, -67.9) * mm});
            skLineSegment(sketch, "E956", {"start": v(39.18, -67.9) * mm, "end": v(39.27, -68.1) * mm});
            skLineSegment(sketch, "E957", {"start": v(39.27, -68.1) * mm, "end": v(39.46, -68.57) * mm});
            skLineSegment(sketch, "E958", {"start": v(39.46, -68.57) * mm, "end": v(39.82, -69.6) * mm});
            skLineSegment(sketch, "E959", {"start": v(39.82, -69.6) * mm, "end": v(40.38, -71.9) * mm});
            skLineSegment(sketch, "E960", {"start": v(38.2, -66.2) * mm, "end": v(39.09, -67.73) * mm});
            skArc(sketch, "E961", {"start": v(38.2, -66.2) * mm, "mid": v(40.01, -65.12) * mm, "end": v(41.79, -64) * mm});
            skLineSegment(sketch, "E962", {"start": v(41.79, -64) * mm, "end": v(42.76, -65.48) * mm});
            skLineSegment(sketch, "E963", {"start": v(42.76, -65.48) * mm, "end": v(42.76, -65.49) * mm});
            skLineSegment(sketch, "E964", {"start": v(42.76, -65.49) * mm, "end": v(42.78, -65.5) * mm});
            skLineSegment(sketch, "E965", {"start": v(42.78, -65.5) * mm, "end": v(42.8, -65.54) * mm});
            skLineSegment(sketch, "E966", {"start": v(42.8, -65.54) * mm, "end": v(42.87, -65.63) * mm});
            skLineSegment(sketch, "E967", {"start": v(42.87, -65.63) * mm, "end": v(43, -65.81) * mm});
            skLineSegment(sketch, "E968", {"start": v(43, -65.81) * mm, "end": v(43.34, -66.2) * mm});
            skLineSegment(sketch, "E969", {"start": v(43.34, -66.2) * mm, "end": v(44.1, -66.97) * mm});
            skLineSegment(sketch, "E970", {"start": v(44.1, -66.97) * mm, "end": v(45.89, -68.5) * mm});
            skArc(sketch, "E971", {"start": v(45.89, -68.5) * mm, "mid": v(46.97, -67.77) * mm, "end": v(48.04, -67.02) * mm});
            skLineSegment(sketch, "E972", {"start": v(46.3, -63.02) * mm, "end": v(46.3, -63.03) * mm});
            skLineSegment(sketch, "E973", {"start": v(46.3, -63.03) * mm, "end": v(46.32, -63.05) * mm});
            skLineSegment(sketch, "E974", {"start": v(46.32, -63.05) * mm, "end": v(46.34, -63.1) * mm});
            skLineSegment(sketch, "E975", {"start": v(46.34, -63.1) * mm, "end": v(46.4, -63.18) * mm});
            skLineSegment(sketch, "E976", {"start": v(46.4, -63.18) * mm, "end": v(46.52, -63.38) * mm});
            skLineSegment(sketch, "E977", {"start": v(46.52, -63.38) * mm, "end": v(46.76, -63.81) * mm});
            skLineSegment(sketch, "E978", {"start": v(46.76, -63.81) * mm, "end": v(47.23, -64.8) * mm});
            skLineSegment(sketch, "E979", {"start": v(47.23, -64.8) * mm, "end": v(48.04, -67.02) * mm});
            skLineSegment(sketch, "E980", {"start": v(45.25, -61.6) * mm, "end": v(46.3, -63.02) * mm});
            skArc(sketch, "E981", {"start": v(45.25, -61.6) * mm, "mid": v(46.93, -60.33) * mm, "end": v(48.57, -59) * mm});
            skLineSegment(sketch, "E982", {"start": v(48.57, -59) * mm, "end": v(49.7, -60.38) * mm});
            skLineSegment(sketch, "E983", {"start": v(49.7, -60.38) * mm, "end": v(49.7, -60.38) * mm});
            skLineSegment(sketch, "E984", {"start": v(49.7, -60.38) * mm, "end": v(49.72, -60.4) * mm});
            skLineSegment(sketch, "E985", {"start": v(49.72, -60.4) * mm, "end": v(49.75, -60.44) * mm});
            skLineSegment(sketch, "E986", {"start": v(49.75, -60.44) * mm, "end": v(49.83, -60.52) * mm});
            skLineSegment(sketch, "E987", {"start": v(49.83, -60.52) * mm, "end": v(49.99, -60.68) * mm});
            skLineSegment(sketch, "E988", {"start": v(49.99, -60.68) * mm, "end": v(50.35, -61.02) * mm});
            skLineSegment(sketch, "E989", {"start": v(50.35, -61.02) * mm, "end": v(51.2, -61.71) * mm});
            skLineSegment(sketch, "E990", {"start": v(51.2, -61.71) * mm, "end": v(53.14, -63.04) * mm});
            skArc(sketch, "E991", {"start": v(53.14, -63.04) * mm, "mid": v(54.14, -62.2) * mm, "end": v(55.12, -61.33) * mm});
            skLineSegment(sketch, "E992", {"start": v(52.95, -57.55) * mm, "end": v(52.95, -57.55) * mm});
            skLineSegment(sketch, "E993", {"start": v(52.95, -57.55) * mm, "end": v(52.97, -57.57) * mm});
            skLineSegment(sketch, "E994", {"start": v(52.97, -57.57) * mm, "end": v(53, -57.6) * mm});
            skLineSegment(sketch, "E995", {"start": v(53, -57.6) * mm, "end": v(53.07, -57.7) * mm});
            skLineSegment(sketch, "E996", {"start": v(53.07, -57.7) * mm, "end": v(53.2, -57.87) * mm});
            skLineSegment(sketch, "E997", {"start": v(53.2, -57.87) * mm, "end": v(53.5, -58.28) * mm});
            skLineSegment(sketch, "E998", {"start": v(53.5, -58.28) * mm, "end": v(54.07, -59.21) * mm});
            skLineSegment(sketch, "E999", {"start": v(54.07, -59.21) * mm, "end": v(55.12, -61.33) * mm});
            skLineSegment(sketch, "E1000", {"start": v(51.75, -56.24) * mm, "end": v(52.95, -57.55) * mm});
            skArc(sketch, "E1001", {"start": v(51.75, -56.24) * mm, "mid": v(53.28, -54.8) * mm, "end": v(54.77, -53.3) * mm});
            skLineSegment(sketch, "E1002", {"start": v(54.77, -53.3) * mm, "end": v(56.03, -54.54) * mm});
            skLineSegment(sketch, "E1003", {"start": v(56.03, -54.54) * mm, "end": v(56.04, -54.55) * mm});
            skLineSegment(sketch, "E1004", {"start": v(56.04, -54.55) * mm, "end": v(56.06, -54.56) * mm});
            skLineSegment(sketch, "E1005", {"start": v(56.06, -54.56) * mm, "end": v(56.1, -54.6) * mm});
            skLineSegment(sketch, "E1006", {"start": v(56.1, -54.6) * mm, "end": v(56.18, -54.67) * mm});
            skLineSegment(sketch, "E1007", {"start": v(56.18, -54.67) * mm, "end": v(56.35, -54.81) * mm});
            skLineSegment(sketch, "E1008", {"start": v(56.35, -54.81) * mm, "end": v(56.76, -55.11) * mm});
            skLineSegment(sketch, "E1009", {"start": v(56.76, -55.11) * mm, "end": v(57.67, -55.7) * mm});
            skLineSegment(sketch, "E1010", {"start": v(57.67, -55.7) * mm, "end": v(59.75, -56.82) * mm});
            skArc(sketch, "E1011", {"start": v(59.75, -56.82) * mm, "mid": v(60.65, -55.86) * mm, "end": v(61.52, -54.9) * mm});
            skLineSegment(sketch, "E1012", {"start": v(58.95, -51.37) * mm, "end": v(58.96, -51.38) * mm});
            skLineSegment(sketch, "E1013", {"start": v(58.96, -51.38) * mm, "end": v(58.97, -51.4) * mm});
            skLineSegment(sketch, "E1014", {"start": v(58.97, -51.4) * mm, "end": v(59.01, -51.43) * mm});
            skLineSegment(sketch, "E1015", {"start": v(59.01, -51.43) * mm, "end": v(59.1, -51.5) * mm});
            skLineSegment(sketch, "E1016", {"start": v(59.1, -51.5) * mm, "end": v(59.25, -51.67) * mm});
            skLineSegment(sketch, "E1017", {"start": v(59.25, -51.67) * mm, "end": v(59.58, -52.04) * mm});
            skLineSegment(sketch, "E1018", {"start": v(59.58, -52.04) * mm, "end": v(60.25, -52.9) * mm});
            skLineSegment(sketch, "E1019", {"start": v(60.25, -52.9) * mm, "end": v(61.52, -54.9) * mm});
            skLineSegment(sketch, "E1020", {"start": v(57.62, -50.21) * mm, "end": v(58.95, -51.37) * mm});
            skArc(sketch, "E1021", {"start": v(57.62, -50.21) * mm, "mid": v(58.98, -48.6) * mm, "end": v(60.3, -46.96) * mm});
            skLineSegment(sketch, "E1022", {"start": v(60.3, -46.96) * mm, "end": v(61.7, -48.05) * mm});
            skLineSegment(sketch, "E1023", {"start": v(61.7, -48.05) * mm, "end": v(61.7, -48.05) * mm});
            skLineSegment(sketch, "E1024", {"start": v(61.7, -48.05) * mm, "end": v(61.72, -48.07) * mm});
            skLineSegment(sketch, "E1025", {"start": v(61.72, -48.07) * mm, "end": v(61.76, -48.1) * mm});
            skLineSegment(sketch, "E1026", {"start": v(61.76, -48.1) * mm, "end": v(61.85, -48.16) * mm});
            skLineSegment(sketch, "E1027", {"start": v(61.85, -48.16) * mm, "end": v(62.04, -48.28) * mm});
            skLineSegment(sketch, "E1028", {"start": v(62.04, -48.28) * mm, "end": v(62.47, -48.54) * mm});
            skLineSegment(sketch, "E1029", {"start": v(62.47, -48.54) * mm, "end": v(63.44, -49.03) * mm});
            skLineSegment(sketch, "E1030", {"start": v(63.44, -49.03) * mm, "end": v(65.64, -49.9) * mm});
            skArc(sketch, "E1031", {"start": v(65.64, -49.9) * mm, "mid": v(66.42, -48.85) * mm, "end": v(67.19, -47.8) * mm});
            skLineSegment(sketch, "E1032", {"start": v(64.24, -44.58) * mm, "end": v(64.25, -44.58) * mm});
            skLineSegment(sketch, "E1033", {"start": v(64.25, -44.58) * mm, "end": v(64.27, -44.6) * mm});
            skLineSegment(sketch, "E1034", {"start": v(64.27, -44.6) * mm, "end": v(64.3, -44.63) * mm});
            skLineSegment(sketch, "E1035", {"start": v(64.3, -44.63) * mm, "end": v(64.4, -44.7) * mm});
            skLineSegment(sketch, "E1036", {"start": v(64.4, -44.7) * mm, "end": v(64.57, -44.84) * mm});
            skLineSegment(sketch, "E1037", {"start": v(64.57, -44.84) * mm, "end": v(64.94, -45.17) * mm});
            skLineSegment(sketch, "E1038", {"start": v(64.94, -45.17) * mm, "end": v(65.7, -45.95) * mm});
            skLineSegment(sketch, "E1039", {"start": v(65.7, -45.95) * mm, "end": v(67.19, -47.8) * mm});
            skLineSegment(sketch, "E1040", {"start": v(62.79, -43.57) * mm, "end": v(64.24, -44.58) * mm});
            skArc(sketch, "E1041", {"start": v(62.79, -43.57) * mm, "mid": v(63.96, -41.82) * mm, "end": v(65.1, -40.04) * mm});
            skLineSegment(sketch, "E1042", {"start": v(65.1, -40.04) * mm, "end": v(66.6, -40.97) * mm});
            skLineSegment(sketch, "E1043", {"start": v(66.6, -40.97) * mm, "end": v(66.6, -40.98) * mm});
            skLineSegment(sketch, "E1044", {"start": v(66.6, -40.98) * mm, "end": v(66.63, -40.99) * mm});
            skLineSegment(sketch, "E1045", {"start": v(66.63, -40.99) * mm, "end": v(66.67, -41.01) * mm});
            skLineSegment(sketch, "E1046", {"start": v(66.67, -41.01) * mm, "end": v(66.77, -41.06) * mm});
            skLineSegment(sketch, "E1047", {"start": v(66.77, -41.06) * mm, "end": v(66.97, -41.16) * mm});
            skLineSegment(sketch, "E1048", {"start": v(66.97, -41.16) * mm, "end": v(67.43, -41.37) * mm});
            skLineSegment(sketch, "E1049", {"start": v(67.43, -41.37) * mm, "end": v(68.45, -41.75) * mm});
            skLineSegment(sketch, "E1050", {"start": v(68.45, -41.75) * mm, "end": v(70.72, -42.37) * mm});
            skArc(sketch, "E1051", {"start": v(70.72, -42.37) * mm, "mid": v(71.39, -41.25) * mm, "end": v(72.03, -40.11) * mm});
            skLineSegment(sketch, "E1052", {"start": v(68.75, -37.24) * mm, "end": v(68.76, -37.24) * mm});
            skLineSegment(sketch, "E1053", {"start": v(68.76, -37.24) * mm, "end": v(68.78, -37.25) * mm});
            skLineSegment(sketch, "E1054", {"start": v(68.78, -37.25) * mm, "end": v(68.82, -37.28) * mm});
            skLineSegment(sketch, "E1055", {"start": v(68.82, -37.28) * mm, "end": v(68.92, -37.34) * mm});
            skLineSegment(sketch, "E1056", {"start": v(68.92, -37.34) * mm, "end": v(69.1, -37.46) * mm});
            skLineSegment(sketch, "E1057", {"start": v(69.1, -37.46) * mm, "end": v(69.51, -37.76) * mm});
            skLineSegment(sketch, "E1058", {"start": v(69.51, -37.76) * mm, "end": v(70.35, -38.45) * mm});
            skLineSegment(sketch, "E1059", {"start": v(70.35, -38.45) * mm, "end": v(72.03, -40.11) * mm});
            skLineSegment(sketch, "E1060", {"start": v(67.2, -36.4) * mm, "end": v(68.75, -37.24) * mm});
            skArc(sketch, "E1061", {"start": v(67.2, -36.4) * mm, "mid": v(68.17, -34.53) * mm, "end": v(69.1, -32.64) * mm});
            skLineSegment(sketch, "E1062", {"start": v(69.1, -32.64) * mm, "end": v(70.7, -33.4) * mm});
            skLineSegment(sketch, "E1063", {"start": v(70.7, -33.4) * mm, "end": v(70.7, -33.4) * mm});
            skLineSegment(sketch, "E1064", {"start": v(70.7, -33.4) * mm, "end": v(70.73, -33.4) * mm});
            skLineSegment(sketch, "E1065", {"start": v(70.73, -33.4) * mm, "end": v(70.77, -33.43) * mm});
            skLineSegment(sketch, "E1066", {"start": v(70.77, -33.43) * mm, "end": v(70.87, -33.47) * mm});
            skLineSegment(sketch, "E1067", {"start": v(70.87, -33.47) * mm, "end": v(71.09, -33.55) * mm});
            skLineSegment(sketch, "E1068", {"start": v(71.09, -33.55) * mm, "end": v(71.56, -33.7) * mm});
            skLineSegment(sketch, "E1069", {"start": v(71.56, -33.7) * mm, "end": v(72.62, -33.97) * mm});
            skLineSegment(sketch, "E1070", {"start": v(72.62, -33.97) * mm, "end": v(74.95, -34.34) * mm});
            skArc(sketch, "E1071", {"start": v(74.95, -34.34) * mm, "mid": v(75.49, -33.14) * mm, "end": v(76, -31.94) * mm});
            skLineSegment(sketch, "E1072", {"start": v(72.43, -29.45) * mm, "end": v(72.44, -29.45) * mm});
            skLineSegment(sketch, "E1073", {"start": v(72.44, -29.45) * mm, "end": v(72.46, -29.46) * mm});
            skLineSegment(sketch, "E1074", {"start": v(72.46, -29.46) * mm, "end": v(72.5, -29.48) * mm});
            skLineSegment(sketch, "E1075", {"start": v(72.5, -29.48) * mm, "end": v(72.6, -29.53) * mm});
            skLineSegment(sketch, "E1076", {"start": v(72.6, -29.53) * mm, "end": v(72.8, -29.63) * mm});
            skLineSegment(sketch, "E1077", {"start": v(72.8, -29.63) * mm, "end": v(73.24, -29.88) * mm});
            skLineSegment(sketch, "E1078", {"start": v(73.24, -29.88) * mm, "end": v(74.15, -30.48) * mm});
            skLineSegment(sketch, "E1079", {"start": v(74.15, -30.48) * mm, "end": v(76, -31.94) * mm});
            skLineSegment(sketch, "E1080", {"start": v(70.79, -28.78) * mm, "end": v(72.43, -29.45) * mm});
            skArc(sketch, "E1081", {"start": v(70.79, -28.78) * mm, "mid": v(71.55, -26.82) * mm, "end": v(72.26, -24.84) * mm});
            skLineSegment(sketch, "E1082", {"start": v(72.26, -24.84) * mm, "end": v(73.94, -25.41) * mm});
            skLineSegment(sketch, "E1083", {"start": v(73.94, -25.41) * mm, "end": v(73.95, -25.42) * mm});
            skLineSegment(sketch, "E1084", {"start": v(73.95, -25.42) * mm, "end": v(73.97, -25.42) * mm});
            skLineSegment(sketch, "E1085", {"start": v(73.97, -25.42) * mm, "end": v(74.02, -25.44) * mm});
            skLineSegment(sketch, "E1086", {"start": v(74.02, -25.44) * mm, "end": v(74.12, -25.47) * mm});
            skLineSegment(sketch, "E1087", {"start": v(74.12, -25.47) * mm, "end": v(74.34, -25.52) * mm});
            skLineSegment(sketch, "E1088", {"start": v(74.34, -25.52) * mm, "end": v(74.83, -25.62) * mm});
            skLineSegment(sketch, "E1089", {"start": v(74.83, -25.62) * mm, "end": v(75.91, -25.77) * mm});
            skLineSegment(sketch, "E1090", {"start": v(75.91, -25.77) * mm, "end": v(78.27, -25.88) * mm});
            skArc(sketch, "E1091", {"start": v(78.27, -25.88) * mm, "mid": v(78.67, -24.64) * mm, "end": v(79.05, -23.39) * mm});
            skLineSegment(sketch, "E1092", {"start": v(75.22, -21.3) * mm, "end": v(75.24, -21.3) * mm});
            skLineSegment(sketch, "E1093", {"start": v(75.24, -21.3) * mm, "end": v(75.25, -21.31) * mm});
            skLineSegment(sketch, "E1094", {"start": v(75.25, -21.31) * mm, "end": v(75.3, -21.33) * mm});
            skLineSegment(sketch, "E1095", {"start": v(75.3, -21.33) * mm, "end": v(75.4, -21.36) * mm});
            skLineSegment(sketch, "E1096", {"start": v(75.4, -21.36) * mm, "end": v(75.62, -21.44) * mm});
            skLineSegment(sketch, "E1097", {"start": v(75.62, -21.44) * mm, "end": v(76.08, -21.64) * mm});
            skLineSegment(sketch, "E1098", {"start": v(76.08, -21.64) * mm, "end": v(77.05, -22.13) * mm});
            skLineSegment(sketch, "E1099", {"start": v(77.05, -22.13) * mm, "end": v(79.05, -23.39) * mm});
            skLineSegment(sketch, "E1100", {"start": v(73.52, -20.82) * mm, "end": v(75.22, -21.3) * mm});
            skArc(sketch, "E1101", {"start": v(73.52, -20.82) * mm, "mid": v(74.07, -18.79) * mm, "end": v(74.55, -16.74) * mm});
            skLineSegment(sketch, "E1102", {"start": v(74.55, -16.74) * mm, "end": v(76.28, -17.13) * mm});
            skLineSegment(sketch, "E1103", {"start": v(76.28, -17.13) * mm, "end": v(76.3, -17.13) * mm});
            skLineSegment(sketch, "E1104", {"start": v(76.3, -17.13) * mm, "end": v(76.31, -17.13) * mm});
            skLineSegment(sketch, "E1105", {"start": v(76.31, -17.13) * mm, "end": v(76.36, -17.14) * mm});
            skLineSegment(sketch, "E1106", {"start": v(76.36, -17.14) * mm, "end": v(76.47, -17.16) * mm});
            skLineSegment(sketch, "E1107", {"start": v(76.47, -17.16) * mm, "end": v(76.7, -17.2) * mm});
            skLineSegment(sketch, "E1108", {"start": v(76.7, -17.2) * mm, "end": v(77.2, -17.24) * mm});
            skLineSegment(sketch, "E1109", {"start": v(77.2, -17.24) * mm, "end": v(78.28, -17.27) * mm});
            skLineSegment(sketch, "E1110", {"start": v(78.28, -17.27) * mm, "end": v(80.64, -17.12) * mm});
            skArc(sketch, "E1111", {"start": v(80.64, -17.12) * mm, "mid": v(80.9, -15.83) * mm, "end": v(81.14, -14.55) * mm});
            skLineSegment(sketch, "E1112", {"start": v(77.1, -12.9) * mm, "end": v(77.12, -12.9) * mm});
            skLineSegment(sketch, "E1113", {"start": v(77.12, -12.9) * mm, "end": v(77.14, -12.9) * mm});
            skLineSegment(sketch, "E1114", {"start": v(77.14, -12.9) * mm, "end": v(77.19, -12.92) * mm});
            skLineSegment(sketch, "E1115", {"start": v(77.19, -12.92) * mm, "end": v(77.3, -12.94) * mm});
            skLineSegment(sketch, "E1116", {"start": v(77.3, -12.94) * mm, "end": v(77.52, -13) * mm});
            skLineSegment(sketch, "E1117", {"start": v(77.52, -13) * mm, "end": v(78, -13.14) * mm});
            skLineSegment(sketch, "E1118", {"start": v(78, -13.14) * mm, "end": v(79.01, -13.52) * mm});
            skLineSegment(sketch, "E1119", {"start": v(79.01, -13.52) * mm, "end": v(81.14, -14.55) * mm});
            skLineSegment(sketch, "E1120", {"start": v(75.36, -12.6) * mm, "end": v(77.1, -12.9) * mm});
            skArc(sketch, "E1121", {"start": v(75.36, -12.6) * mm, "mid": v(75.68, -10.53) * mm, "end": v(75.94, -8.44) * mm});
            skLineSegment(sketch, "E1122", {"start": v(75.94, -8.44) * mm, "end": v(77.7, -8.63) * mm});
            skLineSegment(sketch, "E1123", {"start": v(77.7, -8.63) * mm, "end": v(77.71, -8.63) * mm});
            skLineSegment(sketch, "E1124", {"start": v(77.71, -8.63) * mm, "end": v(77.73, -8.63) * mm});
            skLineSegment(sketch, "E1125", {"start": v(77.73, -8.63) * mm, "end": v(77.78, -8.64) * mm});
            skLineSegment(sketch, "E1126", {"start": v(77.78, -8.64) * mm, "end": v(77.9, -8.64) * mm});
            skLineSegment(sketch, "E1127", {"start": v(77.9, -8.64) * mm, "end": v(78.12, -8.65) * mm});
            skLineSegment(sketch, "E1128", {"start": v(78.12, -8.65) * mm, "end": v(78.62, -8.64) * mm});
            skLineSegment(sketch, "E1129", {"start": v(78.62, -8.64) * mm, "end": v(79.7, -8.55) * mm});
            skLineSegment(sketch, "E1130", {"start": v(79.7, -8.55) * mm, "end": v(82.03, -8.14) * mm});
            skArc(sketch, "E1131", {"start": v(82.03, -8.14) * mm, "mid": v(82.15, -6.84) * mm, "end": v(82.25, -5.54) * mm});
            skLineSegment(sketch, "E1132", {"start": v(78.06, -4.34) * mm, "end": v(78.07, -4.34) * mm});
            skLineSegment(sketch, "E1133", {"start": v(78.07, -4.34) * mm, "end": v(78.09, -4.34) * mm});
            skLineSegment(sketch, "E1134", {"start": v(78.09, -4.34) * mm, "end": v(78.14, -4.35) * mm});
            skLineSegment(sketch, "E1135", {"start": v(78.14, -4.35) * mm, "end": v(78.25, -4.36) * mm});
            skLineSegment(sketch, "E1136", {"start": v(78.25, -4.36) * mm, "end": v(78.47, -4.4) * mm});
            skLineSegment(sketch, "E1137", {"start": v(78.47, -4.4) * mm, "end": v(78.96, -4.48) * mm});
            skLineSegment(sketch, "E1138", {"start": v(78.96, -4.48) * mm, "end": v(80.02, -4.75) * mm});
            skLineSegment(sketch, "E1139", {"start": v(80.02, -4.75) * mm, "end": v(82.25, -5.54) * mm});
            skLineSegment(sketch, "E1140", {"start": v(76.29, -4.24) * mm, "end": v(78.06, -4.34) * mm});
            skCircle(sketch, "E1141", {"center": v(0, 0) * mm, "radius": 101.6 * mm});
            skPoint(sketch, "E1142", {"position": v(82.4, 2.24) * mm});
            skSolve(sketch);
        }
        {
            var Q0;
            Q0=makeQuery(id+"F0.imprint","IMPRINT",FACE,{"disambiguationData":[TD([[makeQuery(id+"F0.imprint","IMPRINT",EDGE,{"derivedFrom":sQuery(id+"F0.wireOp",EDGE,"E0")}),-1.0]])]});
            var sketch = newSketch(context, id + "F1", { "sketchPlane" : qUnion([Q0])});
            skCircle(sketch, "E1143", {"center": v(-64.27, -25.4) * mm, "radius": 2.54 * mm});
            skCircle(sketch, "E1144.MirrorC", {"center": v(-64.27, 25.4) * mm, "radius": 2.54 * mm});
            skCircle(sketch, "E1145", {"center": v(-64.27, 0) * mm, "radius": 9.53 * mm});
            skLineSegment(sketch, "E1146", {"start": v(0, 0) * mm, "end": v(-64.27, 0) * mm, "construction": true});
            skArc(sketch, "E1147", {"start": v(75.91, -3.42) * mm, "mid": v(76.28, -1.73) * mm, "end": v(76.4, 0) * mm});
            skLineSegment(sketch, "E1148", {"start": v(76.4, 0) * mm, "end": v(79.35, 0) * mm});
            skLineSegment(sketch, "E1149", {"start": v(79.35, 0) * mm, "end": v(79.48, 0.01) * mm});
            skLineSegment(sketch, "E1150", {"start": v(79.48, 0.01) * mm, "end": v(79.68, 0.05) * mm});
            skLineSegment(sketch, "E1151", {"start": v(79.68, 0.05) * mm, "end": v(80.05, 0.14) * mm});
            skLineSegment(sketch, "E1152", {"start": v(80.05, 0.14) * mm, "end": v(80.82, 0.46) * mm});
            skLineSegment(sketch, "E1153", {"start": v(80.82, 0.46) * mm, "end": v(81.32, 0.72) * mm});
            skLineSegment(sketch, "E1154", {"start": v(81.32, 0.72) * mm, "end": v(81.83, 1.05) * mm});
            skLineSegment(sketch, "E1155", {"start": v(81.83, 1.05) * mm, "end": v(82.37, 1.45) * mm});
            skArc(sketch, "E1156", {"start": v(82.37, 1.45) * mm, "mid": v(82.25, 2.58) * mm, "end": v(82.05, 3.7) * mm});
            skLineSegment(sketch, "E1157", {"start": v(78.74, 4.25) * mm, "end": v(78.87, 4.28) * mm});
            skLineSegment(sketch, "E1158", {"start": v(78.87, 4.28) * mm, "end": v(79.07, 4.3) * mm});
            skLineSegment(sketch, "E1159", {"start": v(79.07, 4.3) * mm, "end": v(79.45, 4.3) * mm});
            skLineSegment(sketch, "E1160", {"start": v(79.45, 4.3) * mm, "end": v(80.28, 4.23) * mm});
            skLineSegment(sketch, "E1161", {"start": v(80.28, 4.23) * mm, "end": v(80.83, 4.11) * mm});
            skLineSegment(sketch, "E1162", {"start": v(80.83, 4.11) * mm, "end": v(81.41, 3.94) * mm});
            skLineSegment(sketch, "E1163", {"start": v(81.41, 3.94) * mm, "end": v(82.05, 3.7) * mm});
            skLineSegment(sketch, "E1164", {"start": v(75.91, 3.42) * mm, "end": v(78.74, 4.25) * mm});
            skArc(sketch, "E1165", {"start": v(75.91, 3.42) * mm, "mid": v(75.3, 5.04) * mm, "end": v(74.48, 6.56) * mm});
            skLineSegment(sketch, "E1166", {"start": v(74.48, 6.56) * mm, "end": v(76.96, 8.16) * mm});
            skLineSegment(sketch, "E1167", {"start": v(76.96, 8.16) * mm, "end": v(77.06, 8.23) * mm});
            skLineSegment(sketch, "E1168", {"start": v(77.06, 8.23) * mm, "end": v(77.2, 8.37) * mm});
            skLineSegment(sketch, "E1169", {"start": v(77.2, 8.37) * mm, "end": v(77.47, 8.65) * mm});
            skLineSegment(sketch, "E1170", {"start": v(77.47, 8.65) * mm, "end": v(77.95, 9.33) * mm});
            skLineSegment(sketch, "E1171", {"start": v(77.95, 9.33) * mm, "end": v(78.22, 9.82) * mm});
            skLineSegment(sketch, "E1172", {"start": v(78.22, 9.82) * mm, "end": v(78.47, 10.37) * mm});
            skLineSegment(sketch, "E1173", {"start": v(78.47, 10.37) * mm, "end": v(78.72, 11) * mm});
            skArc(sketch, "E1174", {"start": v(78.72, 11) * mm, "mid": v(78, 11.9) * mm, "end": v(77.22, 12.73) * mm});
            skLineSegment(sketch, "E1175", {"start": v(74.15, 11.4) * mm, "end": v(74.24, 11.5) * mm});
            skLineSegment(sketch, "E1176", {"start": v(74.24, 11.5) * mm, "end": v(74.4, 11.62) * mm});
            skLineSegment(sketch, "E1177", {"start": v(74.4, 11.62) * mm, "end": v(74.71, 11.83) * mm});
            skLineSegment(sketch, "E1178", {"start": v(74.71, 11.83) * mm, "end": v(75.45, 12.21) * mm});
            skLineSegment(sketch, "E1179", {"start": v(75.45, 12.21) * mm, "end": v(75.98, 12.41) * mm});
            skLineSegment(sketch, "E1180", {"start": v(75.98, 12.41) * mm, "end": v(76.56, 12.59) * mm});
            skLineSegment(sketch, "E1181", {"start": v(76.56, 12.59) * mm, "end": v(77.22, 12.73) * mm});
            skLineSegment(sketch, "E1182", {"start": v(72.22, 9.17) * mm, "end": v(74.15, 11.4) * mm});
            skArc(sketch, "E1183", {"start": v(72.22, 9.17) * mm, "mid": v(70.83, 10.2) * mm, "end": v(69.3, 11.04) * mm});
            skLineSegment(sketch, "E1184", {"start": v(69.3, 11.04) * mm, "end": v(70.54, 13.72) * mm});
            skLineSegment(sketch, "E1185", {"start": v(70.54, 13.72) * mm, "end": v(70.58, 13.84) * mm});
            skLineSegment(sketch, "E1186", {"start": v(70.58, 13.84) * mm, "end": v(70.63, 14.04) * mm});
            skLineSegment(sketch, "E1187", {"start": v(70.63, 14.04) * mm, "end": v(70.7, 14.41) * mm});
            skLineSegment(sketch, "E1188", {"start": v(70.7, 14.41) * mm, "end": v(70.73, 15.25) * mm});
            skLineSegment(sketch, "E1189", {"start": v(70.73, 15.25) * mm, "end": v(70.7, 15.8) * mm});
            skLineSegment(sketch, "E1190", {"start": v(70.7, 15.8) * mm, "end": v(70.61, 16.4) * mm});
            skLineSegment(sketch, "E1191", {"start": v(70.61, 16.4) * mm, "end": v(70.47, 17.07) * mm});
            skArc(sketch, "E1192", {"start": v(70.47, 17.07) * mm, "mid": v(69.39, 17.43) * mm, "end": v(68.28, 17.71) * mm});
            skLineSegment(sketch, "E1193", {"start": v(66.42, 14.93) * mm, "end": v(66.44, 15.06) * mm});
            skLineSegment(sketch, "E1194", {"start": v(66.44, 15.06) * mm, "end": v(66.5, 15.25) * mm});
            skLineSegment(sketch, "E1195", {"start": v(66.5, 15.25) * mm, "end": v(66.66, 15.6) * mm});
            skLineSegment(sketch, "E1196", {"start": v(66.66, 15.6) * mm, "end": v(67.08, 16.32) * mm});
            skLineSegment(sketch, "E1197", {"start": v(67.08, 16.32) * mm, "end": v(67.4, 16.77) * mm});
            skLineSegment(sketch, "E1198", {"start": v(67.4, 16.77) * mm, "end": v(67.8, 17.23) * mm});
            skLineSegment(sketch, "E1199", {"start": v(67.8, 17.23) * mm, "end": v(68.28, 17.71) * mm});
            skLineSegment(sketch, "E1200", {"start": v(66, 12.01) * mm, "end": v(66.42, 14.93) * mm});
            skArc(sketch, "E1201", {"start": v(66, 12.01) * mm, "mid": v(64.27, 12.14) * mm, "end": v(62.54, 12.01) * mm});
            skLineSegment(sketch, "E1202", {"start": v(62.54, 12.01) * mm, "end": v(62.12, 14.93) * mm});
            skLineSegment(sketch, "E1203", {"start": v(62.12, 14.93) * mm, "end": v(62.1, 15.06) * mm});
            skLineSegment(sketch, "E1204", {"start": v(62.1, 15.06) * mm, "end": v(62.03, 15.25) * mm});
            skLineSegment(sketch, "E1205", {"start": v(62.03, 15.25) * mm, "end": v(61.88, 15.6) * mm});
            skLineSegment(sketch, "E1206", {"start": v(61.88, 15.6) * mm, "end": v(61.46, 16.32) * mm});
            skLineSegment(sketch, "E1207", {"start": v(61.46, 16.32) * mm, "end": v(61.13, 16.77) * mm});
            skLineSegment(sketch, "E1208", {"start": v(61.13, 16.77) * mm, "end": v(60.73, 17.23) * mm});
            skLineSegment(sketch, "E1209", {"start": v(60.73, 17.23) * mm, "end": v(60.26, 17.71) * mm});
            skArc(sketch, "E1210", {"start": v(60.26, 17.71) * mm, "mid": v(59.15, 17.43) * mm, "end": v(58.07, 17.07) * mm});
            skLineSegment(sketch, "E1211", {"start": v(58, 13.72) * mm, "end": v(57.96, 13.84) * mm});
            skLineSegment(sketch, "E1212", {"start": v(57.96, 13.84) * mm, "end": v(57.9, 14.04) * mm});
            skLineSegment(sketch, "E1213", {"start": v(57.9, 14.04) * mm, "end": v(57.84, 14.41) * mm});
            skLineSegment(sketch, "E1214", {"start": v(57.84, 14.41) * mm, "end": v(57.8, 15.25) * mm});
            skLineSegment(sketch, "E1215", {"start": v(57.8, 15.25) * mm, "end": v(57.84, 15.8) * mm});
            skLineSegment(sketch, "E1216", {"start": v(57.84, 15.8) * mm, "end": v(57.93, 16.4) * mm});
            skLineSegment(sketch, "E1217", {"start": v(57.93, 16.4) * mm, "end": v(58.07, 17.07) * mm});
            skLineSegment(sketch, "E1218", {"start": v(59.23, 11.04) * mm, "end": v(58, 13.72) * mm});
            skArc(sketch, "E1219", {"start": v(59.23, 11.04) * mm, "mid": v(57.7, 10.2) * mm, "end": v(56.32, 9.17) * mm});
            skLineSegment(sketch, "E1220", {"start": v(56.32, 9.17) * mm, "end": v(54.39, 11.4) * mm});
            skLineSegment(sketch, "E1221", {"start": v(54.39, 11.4) * mm, "end": v(54.3, 11.5) * mm});
            skLineSegment(sketch, "E1222", {"start": v(54.3, 11.5) * mm, "end": v(54.14, 11.62) * mm});
            skLineSegment(sketch, "E1223", {"start": v(54.14, 11.62) * mm, "end": v(53.83, 11.83) * mm});
            skLineSegment(sketch, "E1224", {"start": v(53.83, 11.83) * mm, "end": v(53.08, 12.21) * mm});
            skLineSegment(sketch, "E1225", {"start": v(53.08, 12.21) * mm, "end": v(52.56, 12.41) * mm});
            skLineSegment(sketch, "E1226", {"start": v(52.56, 12.41) * mm, "end": v(51.98, 12.59) * mm});
            skLineSegment(sketch, "E1227", {"start": v(51.98, 12.59) * mm, "end": v(51.32, 12.73) * mm});
            skArc(sketch, "E1228", {"start": v(51.32, 12.73) * mm, "mid": v(50.54, 11.9) * mm, "end": v(49.82, 11) * mm});
            skLineSegment(sketch, "E1229", {"start": v(51.58, 8.16) * mm, "end": v(51.48, 8.23) * mm});
            skLineSegment(sketch, "E1230", {"start": v(51.48, 8.23) * mm, "end": v(51.33, 8.37) * mm});
            skLineSegment(sketch, "E1231", {"start": v(51.33, 8.37) * mm, "end": v(51.07, 8.65) * mm});
            skLineSegment(sketch, "E1232", {"start": v(51.07, 8.65) * mm, "end": v(50.6, 9.33) * mm});
            skLineSegment(sketch, "E1233", {"start": v(50.6, 9.33) * mm, "end": v(50.32, 9.82) * mm});
            skLineSegment(sketch, "E1234", {"start": v(50.32, 9.82) * mm, "end": v(50.06, 10.37) * mm});
            skLineSegment(sketch, "E1235", {"start": v(50.06, 10.37) * mm, "end": v(49.82, 11) * mm});
            skLineSegment(sketch, "E1236", {"start": v(54.06, 6.56) * mm, "end": v(51.58, 8.16) * mm});
            skArc(sketch, "E1237", {"start": v(54.06, 6.56) * mm, "mid": v(53.23, 5.04) * mm, "end": v(52.62, 3.42) * mm});
            skLineSegment(sketch, "E1238", {"start": v(52.62, 3.42) * mm, "end": v(49.8, 4.25) * mm});
            skLineSegment(sketch, "E1239", {"start": v(49.8, 4.25) * mm, "end": v(49.67, 4.28) * mm});
            skLineSegment(sketch, "E1240", {"start": v(49.67, 4.28) * mm, "end": v(49.47, 4.3) * mm});
            skLineSegment(sketch, "E1241", {"start": v(49.47, 4.3) * mm, "end": v(49.09, 4.3) * mm});
            skLineSegment(sketch, "E1242", {"start": v(49.09, 4.3) * mm, "end": v(48.26, 4.23) * mm});
            skLineSegment(sketch, "E1243", {"start": v(48.26, 4.23) * mm, "end": v(47.7, 4.11) * mm});
            skLineSegment(sketch, "E1244", {"start": v(47.7, 4.11) * mm, "end": v(47.13, 3.94) * mm});
            skLineSegment(sketch, "E1245", {"start": v(47.13, 3.94) * mm, "end": v(46.49, 3.7) * mm});
            skArc(sketch, "E1246", {"start": v(46.49, 3.7) * mm, "mid": v(46.3, 2.58) * mm, "end": v(46.16, 1.45) * mm});
            skLineSegment(sketch, "E1247", {"start": v(49.18, 0) * mm, "end": v(49.05, 0.01) * mm});
            skLineSegment(sketch, "E1248", {"start": v(49.05, 0.01) * mm, "end": v(48.86, 0.05) * mm});
            skLineSegment(sketch, "E1249", {"start": v(48.86, 0.05) * mm, "end": v(48.49, 0.14) * mm});
            skLineSegment(sketch, "E1250", {"start": v(48.49, 0.14) * mm, "end": v(47.72, 0.46) * mm});
            skLineSegment(sketch, "E1251", {"start": v(47.72, 0.46) * mm, "end": v(47.22, 0.72) * mm});
            skLineSegment(sketch, "E1252", {"start": v(47.22, 0.72) * mm, "end": v(46.7, 1.05) * mm});
            skLineSegment(sketch, "E1253", {"start": v(46.7, 1.05) * mm, "end": v(46.16, 1.45) * mm});
            skLineSegment(sketch, "E1254", {"start": v(52.13, 0) * mm, "end": v(49.18, 0) * mm});
            skArc(sketch, "E1255", {"start": v(52.13, 0) * mm, "mid": v(52.26, -1.73) * mm, "end": v(52.62, -3.42) * mm});
            skLineSegment(sketch, "E1256", {"start": v(52.62, -3.42) * mm, "end": v(49.8, -4.25) * mm});
            skLineSegment(sketch, "E1257", {"start": v(49.8, -4.25) * mm, "end": v(49.67, -4.3) * mm});
            skLineSegment(sketch, "E1258", {"start": v(49.67, -4.3) * mm, "end": v(49.5, -4.38) * mm});
            skLineSegment(sketch, "E1259", {"start": v(49.5, -4.38) * mm, "end": v(49.17, -4.58) * mm});
            skLineSegment(sketch, "E1260", {"start": v(49.17, -4.58) * mm, "end": v(48.51, -5.1) * mm});
            skLineSegment(sketch, "E1261", {"start": v(48.51, -5.1) * mm, "end": v(48.11, -5.5) * mm});
            skLineSegment(sketch, "E1262", {"start": v(48.11, -5.5) * mm, "end": v(47.72, -5.95) * mm});
            skLineSegment(sketch, "E1263", {"start": v(47.72, -5.95) * mm, "end": v(47.3, -6.5) * mm});
            skArc(sketch, "E1264", {"start": v(47.3, -6.5) * mm, "mid": v(47.75, -7.55) * mm, "end": v(48.25, -8.57) * mm});
            skLineSegment(sketch, "E1265", {"start": v(51.58, -8.16) * mm, "end": v(51.46, -8.22) * mm});
            skLineSegment(sketch, "E1266", {"start": v(51.46, -8.22) * mm, "end": v(51.28, -8.3) * mm});
            skLineSegment(sketch, "E1267", {"start": v(51.28, -8.3) * mm, "end": v(50.92, -8.41) * mm});
            skLineSegment(sketch, "E1268", {"start": v(50.92, -8.41) * mm, "end": v(50.1, -8.56) * mm});
            skLineSegment(sketch, "E1269", {"start": v(50.1, -8.56) * mm, "end": v(49.54, -8.6) * mm});
            skLineSegment(sketch, "E1270", {"start": v(49.54, -8.6) * mm, "end": v(48.93, -8.61) * mm});
            skLineSegment(sketch, "E1271", {"start": v(48.93, -8.61) * mm, "end": v(48.25, -8.57) * mm});
            skLineSegment(sketch, "E1272", {"start": v(54.06, -6.56) * mm, "end": v(51.58, -8.16) * mm});
            skArc(sketch, "E1273", {"start": v(54.06, -6.56) * mm, "mid": v(55.1, -7.95) * mm, "end": v(56.32, -9.17) * mm});
            skLineSegment(sketch, "E1274", {"start": v(56.32, -9.17) * mm, "end": v(54.39, -11.4) * mm});
            skLineSegment(sketch, "E1275", {"start": v(54.39, -11.4) * mm, "end": v(54.31, -11.5) * mm});
            skLineSegment(sketch, "E1276", {"start": v(54.31, -11.5) * mm, "end": v(54.21, -11.67) * mm});
            skLineSegment(sketch, "E1277", {"start": v(54.21, -11.67) * mm, "end": v(54.04, -12.02) * mm});
            skLineSegment(sketch, "E1278", {"start": v(54.04, -12.02) * mm, "end": v(53.77, -12.8) * mm});
            skLineSegment(sketch, "E1279", {"start": v(53.77, -12.8) * mm, "end": v(53.65, -13.36) * mm});
            skLineSegment(sketch, "E1280", {"start": v(53.65, -13.36) * mm, "end": v(53.56, -13.96) * mm});
            skLineSegment(sketch, "E1281", {"start": v(53.56, -13.96) * mm, "end": v(53.5, -14.63) * mm});
            skArc(sketch, "E1282", {"start": v(53.5, -14.63) * mm, "mid": v(54.45, -15.28) * mm, "end": v(55.43, -15.87) * mm});
            skLineSegment(sketch, "E1283", {"start": v(58, -13.72) * mm, "end": v(57.94, -13.83) * mm});
            skLineSegment(sketch, "E1284", {"start": v(57.94, -13.83) * mm, "end": v(57.83, -14) * mm});
            skLineSegment(sketch, "E1285", {"start": v(57.83, -14) * mm, "end": v(57.58, -14.3) * mm});
            skLineSegment(sketch, "E1286", {"start": v(57.58, -14.3) * mm, "end": v(56.98, -14.87) * mm});
            skLineSegment(sketch, "E1287", {"start": v(56.98, -14.87) * mm, "end": v(56.53, -15.2) * mm});
            skLineSegment(sketch, "E1288", {"start": v(56.53, -15.2) * mm, "end": v(56.02, -15.54) * mm});
            skLineSegment(sketch, "E1289", {"start": v(56.02, -15.54) * mm, "end": v(55.43, -15.87) * mm});
            skLineSegment(sketch, "E1290", {"start": v(59.23, -11.04) * mm, "end": v(58, -13.72) * mm});
            skArc(sketch, "E1291", {"start": v(59.23, -11.04) * mm, "mid": v(60.85, -11.64) * mm, "end": v(62.54, -12.01) * mm});
            skLineSegment(sketch, "E1292", {"start": v(62.54, -12.01) * mm, "end": v(62.12, -14.93) * mm});
            skLineSegment(sketch, "E1293", {"start": v(62.12, -14.93) * mm, "end": v(62.11, -15.06) * mm});
            skLineSegment(sketch, "E1294", {"start": v(62.11, -15.06) * mm, "end": v(62.12, -15.26) * mm});
            skLineSegment(sketch, "E1295", {"start": v(62.12, -15.26) * mm, "end": v(62.17, -15.64) * mm});
            skLineSegment(sketch, "E1296", {"start": v(62.17, -15.64) * mm, "end": v(62.36, -16.45) * mm});
            skLineSegment(sketch, "E1297", {"start": v(62.36, -16.45) * mm, "end": v(62.56, -16.98) * mm});
            skLineSegment(sketch, "E1298", {"start": v(62.56, -16.98) * mm, "end": v(62.8, -17.53) * mm});
            skLineSegment(sketch, "E1299", {"start": v(62.8, -17.53) * mm, "end": v(63.13, -18.13) * mm});
            skArc(sketch, "E1300", {"start": v(63.13, -18.13) * mm, "mid": v(64.27, -18.16) * mm, "end": v(65.4, -18.13) * mm});
            skLineSegment(sketch, "E1301", {"start": v(66.42, -14.93) * mm, "end": v(66.42, -15.06) * mm});
            skLineSegment(sketch, "E1302", {"start": v(66.42, -15.06) * mm, "end": v(66.42, -15.26) * mm});
            skLineSegment(sketch, "E1303", {"start": v(66.42, -15.26) * mm, "end": v(66.37, -15.64) * mm});
            skLineSegment(sketch, "E1304", {"start": v(66.37, -15.64) * mm, "end": v(66.17, -16.45) * mm});
            skLineSegment(sketch, "E1305", {"start": v(66.17, -16.45) * mm, "end": v(65.98, -16.98) * mm});
            skLineSegment(sketch, "E1306", {"start": v(65.98, -16.98) * mm, "end": v(65.73, -17.53) * mm});
            skLineSegment(sketch, "E1307", {"start": v(65.73, -17.53) * mm, "end": v(65.4, -18.13) * mm});
            skLineSegment(sketch, "E1308", {"start": v(66, -12.01) * mm, "end": v(66.42, -14.93) * mm});
            skArc(sketch, "E1309", {"start": v(66, -12.01) * mm, "mid": v(67.69, -11.64) * mm, "end": v(69.3, -11.04) * mm});
            skLineSegment(sketch, "E1310", {"start": v(69.3, -11.04) * mm, "end": v(70.54, -13.72) * mm});
            skLineSegment(sketch, "E1311", {"start": v(70.54, -13.72) * mm, "end": v(70.6, -13.83) * mm});
            skLineSegment(sketch, "E1312", {"start": v(70.6, -13.83) * mm, "end": v(70.71, -14) * mm});
            skLineSegment(sketch, "E1313", {"start": v(70.71, -14) * mm, "end": v(70.95, -14.3) * mm});
            skLineSegment(sketch, "E1314", {"start": v(70.95, -14.3) * mm, "end": v(71.56, -14.87) * mm});
            skLineSegment(sketch, "E1315", {"start": v(71.56, -14.87) * mm, "end": v(72, -15.2) * mm});
            skLineSegment(sketch, "E1316", {"start": v(72, -15.2) * mm, "end": v(72.51, -15.54) * mm});
            skLineSegment(sketch, "E1317", {"start": v(72.51, -15.54) * mm, "end": v(73.1, -15.87) * mm});
            skArc(sketch, "E1318", {"start": v(73.1, -15.87) * mm, "mid": v(74.09, -15.28) * mm, "end": v(75.03, -14.63) * mm});
            skLineSegment(sketch, "E1319", {"start": v(74.15, -11.4) * mm, "end": v(74.22, -11.5) * mm});
            skLineSegment(sketch, "E1320", {"start": v(74.22, -11.5) * mm, "end": v(74.33, -11.67) * mm});
            skLineSegment(sketch, "E1321", {"start": v(74.33, -11.67) * mm, "end": v(74.5, -12.02) * mm});
            skLineSegment(sketch, "E1322", {"start": v(74.5, -12.02) * mm, "end": v(74.76, -12.8) * mm});
            skLineSegment(sketch, "E1323", {"start": v(74.76, -12.8) * mm, "end": v(74.89, -13.36) * mm});
            skLineSegment(sketch, "E1324", {"start": v(74.89, -13.36) * mm, "end": v(74.98, -13.96) * mm});
            skLineSegment(sketch, "E1325", {"start": v(74.98, -13.96) * mm, "end": v(75.03, -14.63) * mm});
            skLineSegment(sketch, "E1326", {"start": v(72.22, -9.17) * mm, "end": v(74.15, -11.4) * mm});
            skArc(sketch, "E1327", {"start": v(72.22, -9.17) * mm, "mid": v(73.44, -7.95) * mm, "end": v(74.48, -6.56) * mm});
            skLineSegment(sketch, "E1328", {"start": v(74.48, -6.56) * mm, "end": v(76.96, -8.16) * mm});
            skLineSegment(sketch, "E1329", {"start": v(76.96, -8.16) * mm, "end": v(77.07, -8.22) * mm});
            skLineSegment(sketch, "E1330", {"start": v(77.07, -8.22) * mm, "end": v(77.26, -8.3) * mm});
            skLineSegment(sketch, "E1331", {"start": v(77.26, -8.3) * mm, "end": v(77.62, -8.41) * mm});
            skLineSegment(sketch, "E1332", {"start": v(77.62, -8.41) * mm, "end": v(78.44, -8.56) * mm});
            skLineSegment(sketch, "E1333", {"start": v(78.44, -8.56) * mm, "end": v(79, -8.6) * mm});
            skLineSegment(sketch, "E1334", {"start": v(79, -8.6) * mm, "end": v(79.6, -8.61) * mm});
            skLineSegment(sketch, "E1335", {"start": v(79.6, -8.61) * mm, "end": v(80.28, -8.57) * mm});
            skArc(sketch, "E1336", {"start": v(80.28, -8.57) * mm, "mid": v(80.79, -7.55) * mm, "end": v(81.23, -6.5) * mm});
            skLineSegment(sketch, "E1337", {"start": v(78.74, -4.25) * mm, "end": v(78.86, -4.3) * mm});
            skLineSegment(sketch, "E1338", {"start": v(78.86, -4.3) * mm, "end": v(79.04, -4.38) * mm});
            skLineSegment(sketch, "E1339", {"start": v(79.04, -4.38) * mm, "end": v(79.37, -4.58) * mm});
            skLineSegment(sketch, "E1340", {"start": v(79.37, -4.58) * mm, "end": v(80.02, -5.1) * mm});
            skLineSegment(sketch, "E1341", {"start": v(80.02, -5.1) * mm, "end": v(80.42, -5.5) * mm});
            skLineSegment(sketch, "E1342", {"start": v(80.42, -5.5) * mm, "end": v(80.82, -5.95) * mm});
            skLineSegment(sketch, "E1343", {"start": v(80.82, -5.95) * mm, "end": v(81.23, -6.5) * mm});
            skLineSegment(sketch, "E1344", {"start": v(75.91, -3.42) * mm, "end": v(78.74, -4.25) * mm});
            skLineSegment(sketch, "E1345", {"start": v(0, 0) * mm, "end": v(0, 47.66) * mm, "construction": true});
            skLineSegment(sketch, "E1346.MirrorCS", {"start": v(0, 0) * mm, "end": v(64.27, 0) * mm, "construction": true});
            skSolve(sketch);
        }
        {
            var Q0;
            {var subQ2=sQuery(id+"F1.wireOp",EDGE,"E1147");Q0=makeQuery(id+"F1.imprint","IMPRINT",FACE,{"disambiguationData":[TD([[makeQuery(id+"F1.imprint","IMPRINT",EDGE,{"derivedFrom":subQ2}),1.0]])]});}
            var Q1;
            Q1=makeQuery(id+"F1.imprint","IMPRINT",FACE,{"disambiguationData":[TD([[makeQuery(id+"F1.imprint","IMPRINT",EDGE,{"derivedFrom":sQuery(id+"F1.wireOp",EDGE,"E1143")}),-1.0]])]});
            extrude(context, id + "F2", {"entities" : qUnion([Q0, Q1]), "depth" : 25.4 * mm, "offsetDistance" : 25.4 * mm});
        }
    });
